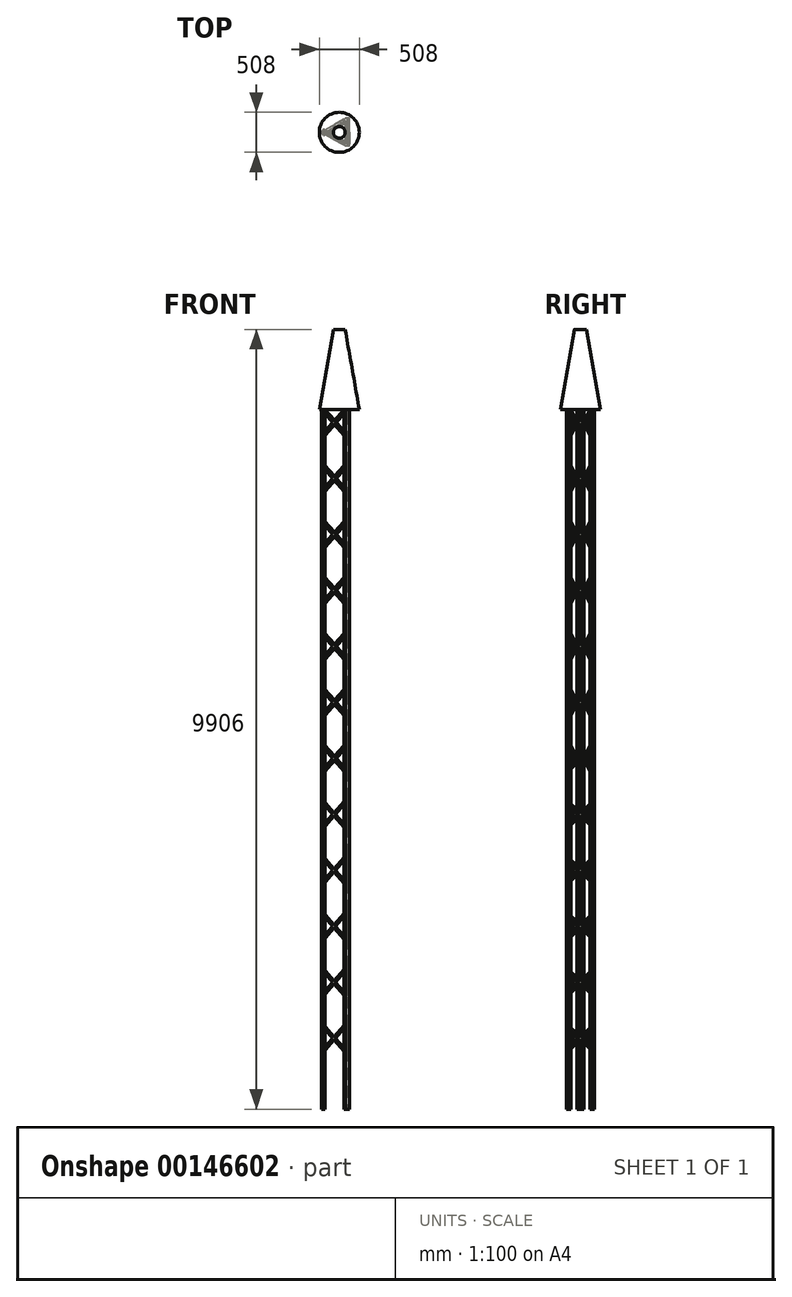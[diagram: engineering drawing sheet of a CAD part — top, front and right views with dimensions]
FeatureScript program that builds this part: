
annotation { "Feature Type Name" : "Feature", "Feature Type Description" : "" }
export const myFeature = defineFeature(function(context is Context, id is Id, definition is map)
    precondition{}
    {
        {
            var Q0;
            Q0=qCreatedBy(makeId("Right.planeOp"),FACE);
            var sketch = newSketch(context, id + "F0", { "sketchPlane" : qUnion([Q0])});
            skLineSegment(sketch, "E0.bottom", {"start": v(0, 1828.8) * mm, "end": v(25.4, 1828.8) * mm});
            skLineSegment(sketch, "E0.top", {"start": v(0, -7061.2) * mm, "end": v(25.4, -7061.2) * mm});
            skLineSegment(sketch, "E0.left", {"start": v(0, 1828.8) * mm, "end": v(0, -7061.2) * mm});
            skLineSegment(sketch, "E0.right", {"start": v(25.4, 1828.8) * mm, "end": v(25.4, -7061.2) * mm});
            skLineSegment(sketch, "E1.bottom", {"start": v(330.2, -7061.2) * mm, "end": v(355.6, -7061.2) * mm});
            skLineSegment(sketch, "E1.top", {"start": v(330.2, 1828.8) * mm, "end": v(355.6, 1828.8) * mm});
            skLineSegment(sketch, "E1.left", {"start": v(330.2, -7061.2) * mm, "end": v(330.2, 1828.8) * mm});
            skLineSegment(sketch, "E1.right", {"start": v(355.6, -7061.2) * mm, "end": v(355.6, 1828.8) * mm});
            skLineSegment(sketch, "E2", {"start": v(25.4, 1828.8) * mm, "end": v(330.2, 1524) * mm});
            skLineSegment(sketch, "E3", {"start": v(25.4, 1803.4) * mm, "end": v(330.2, 1498.6) * mm});
            skLineSegment(sketch, "E4.0.1.0", {"start": v(25.4, 1092.2) * mm, "end": v(330.2, 787.4) * mm});
            skLineSegment(sketch, "E4.0.1.1", {"start": v(25.4, 1117.6) * mm, "end": v(330.2, 812.8) * mm});
            skLineSegment(sketch, "E4.0.2.0", {"start": v(25.4, 381) * mm, "end": v(330.2, 76.2) * mm});
            skLineSegment(sketch, "E4.0.2.1", {"start": v(25.4, 406.4) * mm, "end": v(330.2, 101.6) * mm});
            skLineSegment(sketch, "E4.0.3.0", {"start": v(25.4, -330.2) * mm, "end": v(330.2, -635) * mm});
            skLineSegment(sketch, "E4.0.3.1", {"start": v(25.4, -304.8) * mm, "end": v(330.2, -609.6) * mm});
            skLineSegment(sketch, "E4.0.4.0", {"start": v(25.4, -1041.4) * mm, "end": v(330.2, -1346.2) * mm});
            skLineSegment(sketch, "E4.0.4.1", {"start": v(25.4, -1016) * mm, "end": v(330.2, -1320.8) * mm});
            skLineSegment(sketch, "E4.0.5.0", {"start": v(25.4, -1752.6) * mm, "end": v(330.2, -2057.4) * mm});
            skLineSegment(sketch, "E4.0.5.1", {"start": v(25.4, -1727.2) * mm, "end": v(330.2, -2032) * mm});
            skLineSegment(sketch, "E4.0.6.0", {"start": v(25.4, -2463.8) * mm, "end": v(330.2, -2768.6) * mm});
            skLineSegment(sketch, "E4.0.6.1", {"start": v(25.4, -2438.4) * mm, "end": v(330.2, -2743.2) * mm});
            skLineSegment(sketch, "E4.0.7.0", {"start": v(25.4, -3175) * mm, "end": v(330.2, -3479.8) * mm});
            skLineSegment(sketch, "E4.0.7.1", {"start": v(25.4, -3149.6) * mm, "end": v(330.2, -3454.4) * mm});
            skLineSegment(sketch, "E4.0.8.0", {"start": v(25.4, -3886.2) * mm, "end": v(330.2, -4191) * mm});
            skLineSegment(sketch, "E4.0.8.1", {"start": v(25.4, -3860.8) * mm, "end": v(330.2, -4165.6) * mm});
            skLineSegment(sketch, "E4.0.9.0", {"start": v(25.4, -4597.4) * mm, "end": v(330.2, -4902.2) * mm});
            skLineSegment(sketch, "E4.0.9.1", {"start": v(25.4, -4572) * mm, "end": v(330.2, -4876.8) * mm});
            skLineSegment(sketch, "E4.0.10.0", {"start": v(25.4, -5308.6) * mm, "end": v(330.2, -5613.4) * mm});
            skLineSegment(sketch, "E4.0.10.1", {"start": v(25.4, -5283.2) * mm, "end": v(330.2, -5588) * mm});
            skLineSegment(sketch, "E4.0.11.0", {"start": v(25.4, -6019.8) * mm, "end": v(330.2, -6324.6) * mm});
            skLineSegment(sketch, "E4.0.11.1", {"start": v(25.4, -5994.4) * mm, "end": v(330.2, -6299.2) * mm});
            skLineSegment(sketch, "E4.direction1", {"start": v(330.2, 1498.6) * mm, "end": v(355.6, 1498.6) * mm, "construction": true});
            skLineSegment(sketch, "E4.direction2", {"start": v(330.2, 1498.6) * mm, "end": v(330.2, 787.4) * mm, "construction": true});
            skLineSegment(sketch, "E5", {"start": v(177.8, 1830.45) * mm, "end": v(177.8, 0) * mm});
            skLineSegment(sketch, "E6.MirrorCS", {"start": v(330.2, 1828.8) * mm, "end": v(25.4, 1524) * mm});
            skLineSegment(sketch, "E7.MirrorCS", {"start": v(330.2, 1803.4) * mm, "end": v(25.4, 1498.6) * mm});
            skLineSegment(sketch, "E8.MirrorCS", {"start": v(330.2, 1117.6) * mm, "end": v(25.4, 812.8) * mm});
            skLineSegment(sketch, "E9.MirrorCS", {"start": v(330.2, 1092.2) * mm, "end": v(25.4, 787.4) * mm});
            skLineSegment(sketch, "E10.MirrorCS", {"start": v(330.2, 406.4) * mm, "end": v(25.4, 101.6) * mm});
            skLineSegment(sketch, "E11.MirrorCS", {"start": v(330.2, 381) * mm, "end": v(25.4, 76.2) * mm});
            skLineSegment(sketch, "E12.MirrorCS", {"start": v(330.2, -330.2) * mm, "end": v(25.4, -635) * mm});
            skLineSegment(sketch, "E13.MirrorCS", {"start": v(330.2, -1016) * mm, "end": v(25.4, -1320.8) * mm});
            skLineSegment(sketch, "E14.MirrorCS", {"start": v(330.2, -1041.4) * mm, "end": v(25.4, -1346.2) * mm});
            skLineSegment(sketch, "E15.MirrorCS", {"start": v(330.2, -1727.2) * mm, "end": v(25.4, -2032) * mm});
            skLineSegment(sketch, "E16.MirrorCS", {"start": v(330.2, -1752.6) * mm, "end": v(25.4, -2057.4) * mm});
            skLineSegment(sketch, "E17.MirrorCS", {"start": v(330.2, -304.8) * mm, "end": v(25.4, -609.6) * mm});
            skLineSegment(sketch, "E18.MirrorCS", {"start": v(330.2, -2438.4) * mm, "end": v(25.4, -2743.2) * mm});
            skLineSegment(sketch, "E19.MirrorCS", {"start": v(330.2, -2463.8) * mm, "end": v(25.4, -2768.6) * mm});
            skLineSegment(sketch, "E20.MirrorCS", {"start": v(330.2, -3149.6) * mm, "end": v(25.4, -3454.4) * mm});
            skLineSegment(sketch, "E21.MirrorCS", {"start": v(330.2, -3175) * mm, "end": v(25.4, -3479.8) * mm});
            skLineSegment(sketch, "E22.MirrorCS", {"start": v(330.2, -3860.8) * mm, "end": v(25.4, -4165.6) * mm});
            skLineSegment(sketch, "E23.MirrorCS", {"start": v(330.2, -3886.2) * mm, "end": v(25.4, -4191) * mm});
            skLineSegment(sketch, "E24.MirrorCS", {"start": v(330.2, -4572) * mm, "end": v(25.4, -4876.8) * mm});
            skLineSegment(sketch, "E25.MirrorCS", {"start": v(330.2, -4597.4) * mm, "end": v(25.4, -4902.2) * mm});
            skLineSegment(sketch, "E26.MirrorCS", {"start": v(330.2, -5283.2) * mm, "end": v(25.4, -5588) * mm});
            skLineSegment(sketch, "E27.MirrorCS", {"start": v(330.2, -5308.6) * mm, "end": v(25.4, -5613.4) * mm});
            skLineSegment(sketch, "E28.MirrorCS", {"start": v(330.2, -5994.4) * mm, "end": v(25.4, -6299.2) * mm});
            skLineSegment(sketch, "E29.MirrorCS", {"start": v(330.2, -6019.8) * mm, "end": v(25.4, -6324.6) * mm});
            skSolve(sketch);
        }
        {
            var Q0;
            {var subQ1=sQuery(id+"F0.wireOp",EDGE,"E0.right");var subQ3=sQuery(id+"F0.wireOp",EDGE,"E3");var subQ4=makeQuery(id+"F0.imprint","INTERSECT",VERTEX,{"derivedFrom":[subQ1,subQ3]});Q0=makeQuery(id+"F0.imprint","IMPRINT",FACE,{"disambiguationData":[TD([[makeQuery(id+"F0.imprint","IMPRINT",EDGE,{"disambiguationData":[TD([[subQ4,-1.0]])],"derivedFrom":subQ3}),1.0]])]});}
            var Q1;
            {var subQ30=sQuery(id+"F0.wireOp",EDGE,"E0.bottom");Q1=makeQuery(id+"F0.imprint","IMPRINT",FACE,{"disambiguationData":[TD([[makeQuery(id+"F0.imprint","IMPRINT",EDGE,{"derivedFrom":subQ30}),-1.0]])]});}
            var Q2;
            {var subQ0=sQuery(id+"F0.wireOp",EDGE,"E4.0.1.0");var subQ1=sQuery(id+"F0.wireOp",EDGE,"E0.right");var subQ2=makeQuery(id+"F0.imprint","INTERSECT",VERTEX,{"derivedFrom":[subQ1,subQ0]});Q2=makeQuery(id+"F0.imprint","IMPRINT",FACE,{"disambiguationData":[TD([[makeQuery(id+"F0.imprint","IMPRINT",EDGE,{"disambiguationData":[TD([[subQ2,1.0]])],"derivedFrom":subQ1}),1.0]])]});}
            var Q3;
            {var subQ0=sQuery(id+"F0.wireOp",EDGE,"E8.MirrorCS");var subQ1=sQuery(id+"F0.wireOp",EDGE,"E4.0.1.0");var subQ2=makeQuery(id+"F0.imprint","INTERSECT",VERTEX,{"derivedFrom":[subQ1,subQ0]});Q3=makeQuery(id+"F0.imprint","IMPRINT",FACE,{"disambiguationData":[TD([[makeQuery(id+"F0.imprint","IMPRINT",EDGE,{"disambiguationData":[TD([[subQ2,-1.0]])],"derivedFrom":subQ1}),1.0]])]});}
            var Q4;
            {var subQ0=sQuery(id+"F0.wireOp",EDGE,"E9.MirrorCS");var subQ1=sQuery(id+"F0.wireOp",EDGE,"E4.0.1.1");var subQ2=makeQuery(id+"F0.imprint","INTERSECT",VERTEX,{"derivedFrom":[subQ1,subQ0]});Q4=makeQuery(id+"F0.imprint","IMPRINT",FACE,{"disambiguationData":[TD([[makeQuery(id+"F0.imprint","IMPRINT",EDGE,{"disambiguationData":[TD([[subQ2,1.0]])],"derivedFrom":subQ1}),-1.0]])]});}
            var Q5;
            {var subQ0=sQuery(id+"F0.wireOp",EDGE,"E4.0.1.0");var subQ1=sQuery(id+"F0.wireOp",EDGE,"E1.left");var subQ2=makeQuery(id+"F0.imprint","INTERSECT",VERTEX,{"derivedFrom":[subQ1,subQ0]});Q5=makeQuery(id+"F0.imprint","IMPRINT",FACE,{"disambiguationData":[TD([[makeQuery(id+"F0.imprint","IMPRINT",EDGE,{"disambiguationData":[TD([[subQ2,-1.0]])],"derivedFrom":subQ1}),1.0]])]});}
            var Q6;
            {var subQ0=sQuery(id+"F0.wireOp",EDGE,"E6.MirrorCS");var subQ1=sQuery(id+"F0.wireOp",EDGE,"E3");var subQ2=makeQuery(id+"F0.imprint","INTERSECT",VERTEX,{"derivedFrom":[subQ1,subQ0]});Q6=makeQuery(id+"F0.imprint","IMPRINT",FACE,{"disambiguationData":[TD([[makeQuery(id+"F0.imprint","IMPRINT",EDGE,{"disambiguationData":[TD([[subQ2,-1.0]])],"derivedFrom":subQ1}),1.0]])]});}
            var Q7;
            {var subQ1=sQuery(id+"F0.wireOp",EDGE,"E2");var subQ3=sQuery(id+"F0.wireOp",EDGE,"E7.MirrorCS");var subQ4=makeQuery(id+"F0.imprint","INTERSECT",VERTEX,{"derivedFrom":[subQ1,subQ3]});Q7=makeQuery(id+"F0.imprint","IMPRINT",FACE,{"disambiguationData":[TD([[makeQuery(id+"F0.imprint","IMPRINT",EDGE,{"disambiguationData":[TD([[subQ4,1.0]])],"derivedFrom":subQ1}),-1.0]])]});}
            var Q8;
            {var subQ0=sQuery(id+"F0.wireOp",EDGE,"E2");var subQ1=sQuery(id+"F0.wireOp",EDGE,"E1.left");var subQ2=makeQuery(id+"F0.imprint","INTERSECT",VERTEX,{"derivedFrom":[subQ1,subQ0]});Q8=makeQuery(id+"F0.imprint","IMPRINT",FACE,{"disambiguationData":[TD([[makeQuery(id+"F0.imprint","IMPRINT",EDGE,{"disambiguationData":[TD([[subQ2,1.0]])],"derivedFrom":subQ1}),1.0]])]});}
            var Q9;
            {var subQ42=sQuery(id+"F0.wireOp",EDGE,"E1.bottom");Q9=makeQuery(id+"F0.imprint","IMPRINT",FACE,{"disambiguationData":[TD([[makeQuery(id+"F0.imprint","IMPRINT",EDGE,{"derivedFrom":subQ42}),1.0]])]});}
            var Q10;
            {var subQ0=sQuery(id+"F0.wireOp",EDGE,"E4.0.2.1");var subQ1=sQuery(id+"F0.wireOp",EDGE,"E0.right");var subQ2=makeQuery(id+"F0.imprint","INTERSECT",VERTEX,{"derivedFrom":[subQ1,subQ0]});Q10=makeQuery(id+"F0.imprint","IMPRINT",FACE,{"disambiguationData":[TD([[makeQuery(id+"F0.imprint","IMPRINT",EDGE,{"disambiguationData":[TD([[subQ2,-1.0]])],"derivedFrom":subQ1}),1.0]])]});}
            var Q11;
            {var subQ0=sQuery(id+"F0.wireOp",EDGE,"E4.0.2.1");var subQ1=sQuery(id+"F0.wireOp",EDGE,"E1.left");var subQ2=makeQuery(id+"F0.imprint","INTERSECT",VERTEX,{"derivedFrom":[subQ1,subQ0]});Q11=makeQuery(id+"F0.imprint","IMPRINT",FACE,{"disambiguationData":[TD([[makeQuery(id+"F0.imprint","IMPRINT",EDGE,{"disambiguationData":[TD([[subQ2,1.0]])],"derivedFrom":subQ1}),1.0]])]});}
            var Q12;
            {var subQ0=sQuery(id+"F0.wireOp",EDGE,"E6.MirrorCS");var subQ1=sQuery(id+"F0.wireOp",EDGE,"E0.right");var subQ2=makeQuery(id+"F0.imprint","INTERSECT",VERTEX,{"derivedFrom":[subQ1,subQ0]});Q12=makeQuery(id+"F0.imprint","IMPRINT",FACE,{"disambiguationData":[TD([[makeQuery(id+"F0.imprint","IMPRINT",EDGE,{"disambiguationData":[TD([[subQ2,-1.0]])],"derivedFrom":subQ1}),1.0]])]});}
            var Q13;
            {var subQ0=sQuery(id+"F0.wireOp",EDGE,"E4.0.3.0");var subQ1=sQuery(id+"F0.wireOp",EDGE,"E0.right");var subQ2=makeQuery(id+"F0.imprint","INTERSECT",VERTEX,{"derivedFrom":[subQ1,subQ0]});Q13=makeQuery(id+"F0.imprint","IMPRINT",FACE,{"disambiguationData":[TD([[makeQuery(id+"F0.imprint","IMPRINT",EDGE,{"disambiguationData":[TD([[subQ2,1.0]])],"derivedFrom":subQ1}),1.0]])]});}
            var Q14;
            {var subQ0=sQuery(id+"F0.wireOp",EDGE,"E4.0.3.0");var subQ1=sQuery(id+"F0.wireOp",EDGE,"E1.left");var subQ2=makeQuery(id+"F0.imprint","INTERSECT",VERTEX,{"derivedFrom":[subQ1,subQ0]});Q14=makeQuery(id+"F0.imprint","IMPRINT",FACE,{"disambiguationData":[TD([[makeQuery(id+"F0.imprint","IMPRINT",EDGE,{"disambiguationData":[TD([[subQ2,-1.0]])],"derivedFrom":subQ1}),1.0]])]});}
            var Q15;
            {var subQ0=sQuery(id+"F0.wireOp",EDGE,"E17.MirrorCS");var subQ1=sQuery(id+"F0.wireOp",EDGE,"E4.0.3.0");var subQ2=makeQuery(id+"F0.imprint","INTERSECT",VERTEX,{"derivedFrom":[subQ1,subQ0]});Q15=makeQuery(id+"F0.imprint","IMPRINT",FACE,{"disambiguationData":[TD([[makeQuery(id+"F0.imprint","IMPRINT",EDGE,{"disambiguationData":[TD([[subQ2,-1.0]])],"derivedFrom":subQ1}),1.0]])]});}
            var Q16;
            {var subQ0=sQuery(id+"F0.wireOp",EDGE,"E8.MirrorCS");var subQ1=sQuery(id+"F0.wireOp",EDGE,"E0.right");var subQ2=makeQuery(id+"F0.imprint","INTERSECT",VERTEX,{"derivedFrom":[subQ1,subQ0]});Q16=makeQuery(id+"F0.imprint","IMPRINT",FACE,{"disambiguationData":[TD([[makeQuery(id+"F0.imprint","IMPRINT",EDGE,{"disambiguationData":[TD([[subQ2,-1.0]])],"derivedFrom":subQ1}),1.0]])]});}
            var Q17;
            {var subQ0=sQuery(id+"F0.wireOp",EDGE,"E4.0.2.0");var subQ3=sQuery(id+"F0.wireOp",EDGE,"E10.MirrorCS");var subQ5=makeQuery(id+"F0.imprint","INTERSECT",VERTEX,{"derivedFrom":[subQ3,subQ0]});Q17=makeQuery(id+"F0.imprint","IMPRINT",FACE,{"disambiguationData":[TD([[makeQuery(id+"F0.imprint","IMPRINT",EDGE,{"disambiguationData":[TD([[subQ5,1.0]])],"derivedFrom":subQ3}),1.0]])]});}
            var Q18;
            {var subQ0=sQuery(id+"F0.wireOp",EDGE,"E11.MirrorCS");var subQ1=sQuery(id+"F0.wireOp",EDGE,"E4.0.2.1");var subQ2=makeQuery(id+"F0.imprint","INTERSECT",VERTEX,{"derivedFrom":[subQ1,subQ0]});Q18=makeQuery(id+"F0.imprint","IMPRINT",FACE,{"disambiguationData":[TD([[makeQuery(id+"F0.imprint","IMPRINT",EDGE,{"disambiguationData":[TD([[subQ2,1.0]])],"derivedFrom":subQ1}),-1.0]])]});}
            var Q19;
            {var subQ1=sQuery(id+"F0.wireOp",EDGE,"E1.left");var subQ3=sQuery(id+"F0.wireOp",EDGE,"E7.MirrorCS");var subQ4=makeQuery(id+"F0.imprint","INTERSECT",VERTEX,{"derivedFrom":[subQ1,subQ3]});Q19=makeQuery(id+"F0.imprint","IMPRINT",FACE,{"disambiguationData":[TD([[makeQuery(id+"F0.imprint","IMPRINT",EDGE,{"disambiguationData":[TD([[subQ4,-1.0]])],"derivedFrom":subQ3}),-1.0]])]});}
            var Q20;
            {var subQ0=sQuery(id+"F0.wireOp",EDGE,"E8.MirrorCS");var subQ1=sQuery(id+"F0.wireOp",EDGE,"E1.left");var subQ2=makeQuery(id+"F0.imprint","INTERSECT",VERTEX,{"derivedFrom":[subQ1,subQ0]});Q20=makeQuery(id+"F0.imprint","IMPRINT",FACE,{"disambiguationData":[TD([[makeQuery(id+"F0.imprint","IMPRINT",EDGE,{"disambiguationData":[TD([[subQ2,1.0]])],"derivedFrom":subQ1}),1.0]])]});}
            var Q21;
            {var subQ0=sQuery(id+"F0.wireOp",EDGE,"E10.MirrorCS");var subQ1=sQuery(id+"F0.wireOp",EDGE,"E1.left");var subQ2=makeQuery(id+"F0.imprint","INTERSECT",VERTEX,{"derivedFrom":[subQ1,subQ0]});Q21=makeQuery(id+"F0.imprint","IMPRINT",FACE,{"disambiguationData":[TD([[makeQuery(id+"F0.imprint","IMPRINT",EDGE,{"disambiguationData":[TD([[subQ2,1.0]])],"derivedFrom":subQ1}),1.0]])]});}
            var Q22;
            {var subQ0=sQuery(id+"F0.wireOp",EDGE,"E12.MirrorCS");var subQ1=sQuery(id+"F0.wireOp",EDGE,"E1.left");var subQ2=makeQuery(id+"F0.imprint","INTERSECT",VERTEX,{"derivedFrom":[subQ1,subQ0]});Q22=makeQuery(id+"F0.imprint","IMPRINT",FACE,{"disambiguationData":[TD([[makeQuery(id+"F0.imprint","IMPRINT",EDGE,{"disambiguationData":[TD([[subQ2,-1.0]])],"derivedFrom":subQ1}),1.0]])]});}
            var Q23;
            {var subQ0=sQuery(id+"F0.wireOp",EDGE,"E4.0.4.0");var subQ1=sQuery(id+"F0.wireOp",EDGE,"E0.right");var subQ2=makeQuery(id+"F0.imprint","INTERSECT",VERTEX,{"derivedFrom":[subQ1,subQ0]});Q23=makeQuery(id+"F0.imprint","IMPRINT",FACE,{"disambiguationData":[TD([[makeQuery(id+"F0.imprint","IMPRINT",EDGE,{"disambiguationData":[TD([[subQ2,1.0]])],"derivedFrom":subQ1}),1.0]])]});}
            var Q24;
            {var subQ0=sQuery(id+"F0.wireOp",EDGE,"E4.0.4.0");var subQ1=sQuery(id+"F0.wireOp",EDGE,"E1.left");var subQ2=makeQuery(id+"F0.imprint","INTERSECT",VERTEX,{"derivedFrom":[subQ1,subQ0]});Q24=makeQuery(id+"F0.imprint","IMPRINT",FACE,{"disambiguationData":[TD([[makeQuery(id+"F0.imprint","IMPRINT",EDGE,{"disambiguationData":[TD([[subQ2,-1.0]])],"derivedFrom":subQ1}),1.0]])]});}
            var Q25;
            {var subQ0=sQuery(id+"F0.wireOp",EDGE,"E13.MirrorCS");var subQ1=sQuery(id+"F0.wireOp",EDGE,"E4.0.4.0");var subQ2=makeQuery(id+"F0.imprint","INTERSECT",VERTEX,{"derivedFrom":[subQ1,subQ0]});Q25=makeQuery(id+"F0.imprint","IMPRINT",FACE,{"disambiguationData":[TD([[makeQuery(id+"F0.imprint","IMPRINT",EDGE,{"disambiguationData":[TD([[subQ2,-1.0]])],"derivedFrom":subQ1}),1.0]])]});}
            var Q26;
            {var subQ0=sQuery(id+"F0.wireOp",EDGE,"E10.MirrorCS");var subQ1=sQuery(id+"F0.wireOp",EDGE,"E0.right");var subQ2=makeQuery(id+"F0.imprint","INTERSECT",VERTEX,{"derivedFrom":[subQ1,subQ0]});Q26=makeQuery(id+"F0.imprint","IMPRINT",FACE,{"disambiguationData":[TD([[makeQuery(id+"F0.imprint","IMPRINT",EDGE,{"disambiguationData":[TD([[subQ2,-1.0]])],"derivedFrom":subQ1}),1.0]])]});}
            var Q27;
            {var subQ0=sQuery(id+"F0.wireOp",EDGE,"E13.MirrorCS");var subQ1=sQuery(id+"F0.wireOp",EDGE,"E1.left");var subQ2=makeQuery(id+"F0.imprint","INTERSECT",VERTEX,{"derivedFrom":[subQ1,subQ0]});Q27=makeQuery(id+"F0.imprint","IMPRINT",FACE,{"disambiguationData":[TD([[makeQuery(id+"F0.imprint","IMPRINT",EDGE,{"disambiguationData":[TD([[subQ2,1.0]])],"derivedFrom":subQ1}),1.0]])]});}
            var Q28;
            {var subQ0=sQuery(id+"F0.wireOp",EDGE,"E15.MirrorCS");var subQ1=sQuery(id+"F0.wireOp",EDGE,"E1.left");var subQ2=makeQuery(id+"F0.imprint","INTERSECT",VERTEX,{"derivedFrom":[subQ1,subQ0]});Q28=makeQuery(id+"F0.imprint","IMPRINT",FACE,{"disambiguationData":[TD([[makeQuery(id+"F0.imprint","IMPRINT",EDGE,{"disambiguationData":[TD([[subQ2,1.0]])],"derivedFrom":subQ1}),1.0]])]});}
            var Q29;
            {var subQ0=sQuery(id+"F0.wireOp",EDGE,"E18.MirrorCS");var subQ1=sQuery(id+"F0.wireOp",EDGE,"E1.left");var subQ2=makeQuery(id+"F0.imprint","INTERSECT",VERTEX,{"derivedFrom":[subQ1,subQ0]});Q29=makeQuery(id+"F0.imprint","IMPRINT",FACE,{"disambiguationData":[TD([[makeQuery(id+"F0.imprint","IMPRINT",EDGE,{"disambiguationData":[TD([[subQ2,1.0]])],"derivedFrom":subQ1}),1.0]])]});}
            var Q30;
            {var subQ0=sQuery(id+"F0.wireOp",EDGE,"E4.0.5.0");var subQ1=sQuery(id+"F0.wireOp",EDGE,"E0.right");var subQ2=makeQuery(id+"F0.imprint","INTERSECT",VERTEX,{"derivedFrom":[subQ1,subQ0]});Q30=makeQuery(id+"F0.imprint","IMPRINT",FACE,{"disambiguationData":[TD([[makeQuery(id+"F0.imprint","IMPRINT",EDGE,{"disambiguationData":[TD([[subQ2,1.0]])],"derivedFrom":subQ1}),1.0]])]});}
            var Q31;
            {var subQ0=sQuery(id+"F0.wireOp",EDGE,"E4.0.5.0");var subQ1=sQuery(id+"F0.wireOp",EDGE,"E1.left");var subQ2=makeQuery(id+"F0.imprint","INTERSECT",VERTEX,{"derivedFrom":[subQ1,subQ0]});Q31=makeQuery(id+"F0.imprint","IMPRINT",FACE,{"disambiguationData":[TD([[makeQuery(id+"F0.imprint","IMPRINT",EDGE,{"disambiguationData":[TD([[subQ2,-1.0]])],"derivedFrom":subQ1}),1.0]])]});}
            var Q32;
            {var subQ0=sQuery(id+"F0.wireOp",EDGE,"E15.MirrorCS");var subQ1=sQuery(id+"F0.wireOp",EDGE,"E4.0.5.0");var subQ2=makeQuery(id+"F0.imprint","INTERSECT",VERTEX,{"derivedFrom":[subQ1,subQ0]});Q32=makeQuery(id+"F0.imprint","IMPRINT",FACE,{"disambiguationData":[TD([[makeQuery(id+"F0.imprint","IMPRINT",EDGE,{"disambiguationData":[TD([[subQ2,-1.0]])],"derivedFrom":subQ1}),1.0]])]});}
            var Q33;
            {var subQ0=sQuery(id+"F0.wireOp",EDGE,"E12.MirrorCS");var subQ1=sQuery(id+"F0.wireOp",EDGE,"E0.right");var subQ2=makeQuery(id+"F0.imprint","INTERSECT",VERTEX,{"derivedFrom":[subQ1,subQ0]});Q33=makeQuery(id+"F0.imprint","IMPRINT",FACE,{"disambiguationData":[TD([[makeQuery(id+"F0.imprint","IMPRINT",EDGE,{"disambiguationData":[TD([[subQ2,1.0]])],"derivedFrom":subQ1}),1.0]])]});}
            var Q34;
            {var subQ0=sQuery(id+"F0.wireOp",EDGE,"E4.0.6.0");var subQ1=sQuery(id+"F0.wireOp",EDGE,"E0.right");var subQ2=makeQuery(id+"F0.imprint","INTERSECT",VERTEX,{"derivedFrom":[subQ1,subQ0]});Q34=makeQuery(id+"F0.imprint","IMPRINT",FACE,{"disambiguationData":[TD([[makeQuery(id+"F0.imprint","IMPRINT",EDGE,{"disambiguationData":[TD([[subQ2,1.0]])],"derivedFrom":subQ1}),1.0]])]});}
            var Q35;
            {var subQ0=sQuery(id+"F0.wireOp",EDGE,"E4.0.6.0");var subQ1=sQuery(id+"F0.wireOp",EDGE,"E1.left");var subQ2=makeQuery(id+"F0.imprint","INTERSECT",VERTEX,{"derivedFrom":[subQ1,subQ0]});Q35=makeQuery(id+"F0.imprint","IMPRINT",FACE,{"disambiguationData":[TD([[makeQuery(id+"F0.imprint","IMPRINT",EDGE,{"disambiguationData":[TD([[subQ2,-1.0]])],"derivedFrom":subQ1}),1.0]])]});}
            var Q36;
            {var subQ0=sQuery(id+"F0.wireOp",EDGE,"E18.MirrorCS");var subQ1=sQuery(id+"F0.wireOp",EDGE,"E4.0.6.0");var subQ2=makeQuery(id+"F0.imprint","INTERSECT",VERTEX,{"derivedFrom":[subQ1,subQ0]});Q36=makeQuery(id+"F0.imprint","IMPRINT",FACE,{"disambiguationData":[TD([[makeQuery(id+"F0.imprint","IMPRINT",EDGE,{"disambiguationData":[TD([[subQ2,-1.0]])],"derivedFrom":subQ1}),1.0]])]});}
            var Q37;
            {var subQ0=sQuery(id+"F0.wireOp",EDGE,"E13.MirrorCS");var subQ1=sQuery(id+"F0.wireOp",EDGE,"E0.right");var subQ2=makeQuery(id+"F0.imprint","INTERSECT",VERTEX,{"derivedFrom":[subQ1,subQ0]});Q37=makeQuery(id+"F0.imprint","IMPRINT",FACE,{"disambiguationData":[TD([[makeQuery(id+"F0.imprint","IMPRINT",EDGE,{"disambiguationData":[TD([[subQ2,-1.0]])],"derivedFrom":subQ1}),1.0]])]});}
            var Q38;
            {var subQ0=sQuery(id+"F0.wireOp",EDGE,"E15.MirrorCS");var subQ1=sQuery(id+"F0.wireOp",EDGE,"E0.right");var subQ2=makeQuery(id+"F0.imprint","INTERSECT",VERTEX,{"derivedFrom":[subQ1,subQ0]});Q38=makeQuery(id+"F0.imprint","IMPRINT",FACE,{"disambiguationData":[TD([[makeQuery(id+"F0.imprint","IMPRINT",EDGE,{"disambiguationData":[TD([[subQ2,-1.0]])],"derivedFrom":subQ1}),1.0]])]});}
            var Q39;
            {var subQ0=sQuery(id+"F0.wireOp",EDGE,"E12.MirrorCS");var subQ1=sQuery(id+"F0.wireOp",EDGE,"E4.0.3.1");var subQ2=makeQuery(id+"F0.imprint","INTERSECT",VERTEX,{"derivedFrom":[subQ1,subQ0]});Q39=makeQuery(id+"F0.imprint","IMPRINT",FACE,{"disambiguationData":[TD([[makeQuery(id+"F0.imprint","IMPRINT",EDGE,{"disambiguationData":[TD([[subQ2,1.0]])],"derivedFrom":subQ1}),-1.0]])]});}
            extrude(context, id + "F1", {"entities" : qUnion([Q0, Q1, Q2, Q3, Q4, Q5, Q6, Q7, Q8, Q9, Q10, Q11, Q12, Q13, Q14, Q15, Q16, Q17, Q18, Q19, Q20, Q21, Q22, Q23, Q24, Q25, Q26, Q27, Q28, Q29, Q30, Q31, Q32, Q33, Q34, Q35, Q36, Q37, Q38, Q39]), "depth" : 25.4 * mm});
        }
        {
            var Q0;
            {var subQ0=sQuery(id+"F0.wireOp",EDGE,"E14.MirrorCS");var subQ1=sQuery(id+"F0.wireOp",EDGE,"E4.0.5.0");var subQ2=makeQuery(id+"F0.imprint","INTERSECT",VERTEX,{"derivedFrom":[subQ1,subQ0]});Q0=makeQuery(id+"F0.imprint","IMPRINT",FACE,{"disambiguationData":[TD([[makeQuery(id+"F0.imprint","IMPRINT",EDGE,{"disambiguationData":[TD([[subQ2,-1.0]])],"derivedFrom":subQ1}),1.0]])]});}
            var Q1;
            {var subQ0=sQuery(id+"F0.wireOp",EDGE,"E15.MirrorCS");var subQ1=sQuery(id+"F0.wireOp",EDGE,"E4.0.5.0");var subQ2=makeQuery(id+"F0.imprint","INTERSECT",VERTEX,{"derivedFrom":[subQ1,subQ0]});Q1=makeQuery(id+"F0.imprint","IMPRINT",FACE,{"disambiguationData":[TD([[makeQuery(id+"F0.imprint","IMPRINT",EDGE,{"disambiguationData":[TD([[subQ2,-1.0]])],"derivedFrom":subQ1}),1.0]])]});}
            var Q2;
            {var subQ0=sQuery(id+"F0.wireOp",EDGE,"E16.MirrorCS");var subQ1=sQuery(id+"F0.wireOp",EDGE,"E4.0.5.1");var subQ2=makeQuery(id+"F0.imprint","INTERSECT",VERTEX,{"derivedFrom":[subQ1,subQ0]});Q2=makeQuery(id+"F0.imprint","IMPRINT",FACE,{"disambiguationData":[TD([[makeQuery(id+"F0.imprint","IMPRINT",EDGE,{"disambiguationData":[TD([[subQ2,1.0]])],"derivedFrom":subQ1}),-1.0]])]});}
            var Q3;
            {var subQ0=sQuery(id+"F0.wireOp",EDGE,"E15.MirrorCS");var subQ1=sQuery(id+"F0.wireOp",EDGE,"E4.0.6.0");var subQ2=makeQuery(id+"F0.imprint","INTERSECT",VERTEX,{"derivedFrom":[subQ1,subQ0]});Q3=makeQuery(id+"F0.imprint","IMPRINT",FACE,{"disambiguationData":[TD([[makeQuery(id+"F0.imprint","IMPRINT",EDGE,{"disambiguationData":[TD([[subQ2,-1.0]])],"derivedFrom":subQ1}),1.0]])]});}
            var Q4;
            {var subQ0=sQuery(id+"F0.wireOp",EDGE,"E15.MirrorCS");var subQ1=sQuery(id+"F0.wireOp",EDGE,"E4.0.7.0");var subQ2=makeQuery(id+"F0.imprint","INTERSECT",VERTEX,{"derivedFrom":[subQ1,subQ0]});Q4=makeQuery(id+"F0.imprint","IMPRINT",FACE,{"disambiguationData":[TD([[makeQuery(id+"F0.imprint","IMPRINT",EDGE,{"disambiguationData":[TD([[subQ2,-1.0]])],"derivedFrom":subQ1}),1.0]])]});}
            var Q5;
            {var subQ0=sQuery(id+"F0.wireOp",EDGE,"E15.MirrorCS");var subQ1=sQuery(id+"F0.wireOp",EDGE,"E0.right");var subQ2=makeQuery(id+"F0.imprint","INTERSECT",VERTEX,{"derivedFrom":[subQ1,subQ0]});Q5=makeQuery(id+"F0.imprint","IMPRINT",FACE,{"disambiguationData":[TD([[makeQuery(id+"F0.imprint","IMPRINT",EDGE,{"disambiguationData":[TD([[subQ2,-1.0]])],"derivedFrom":subQ1}),1.0]])]});}
            var Q6;
            {var subQ0=sQuery(id+"F0.wireOp",EDGE,"E4.0.7.0");var subQ1=sQuery(id+"F0.wireOp",EDGE,"E0.right");var subQ2=makeQuery(id+"F0.imprint","INTERSECT",VERTEX,{"derivedFrom":[subQ1,subQ0]});Q6=makeQuery(id+"F0.imprint","IMPRINT",FACE,{"disambiguationData":[TD([[makeQuery(id+"F0.imprint","IMPRINT",EDGE,{"disambiguationData":[TD([[subQ2,1.0]])],"derivedFrom":subQ1}),1.0]])]});}
            var Q7;
            {var subQ0=sQuery(id+"F0.wireOp",EDGE,"E14.MirrorCS");var subQ1=sQuery(id+"F0.wireOp",EDGE,"E4.0.6.0");var subQ2=makeQuery(id+"F0.imprint","INTERSECT",VERTEX,{"derivedFrom":[subQ1,subQ0]});Q7=makeQuery(id+"F0.imprint","IMPRINT",FACE,{"disambiguationData":[TD([[makeQuery(id+"F0.imprint","IMPRINT",EDGE,{"disambiguationData":[TD([[subQ2,-1.0]])],"derivedFrom":subQ1}),1.0]])]});}
            var Q8;
            {var subQ0=sQuery(id+"F0.wireOp",EDGE,"E16.MirrorCS");var subQ1=sQuery(id+"F0.wireOp",EDGE,"E4.0.6.0");var subQ2=makeQuery(id+"F0.imprint","INTERSECT",VERTEX,{"derivedFrom":[subQ1,subQ0]});Q8=makeQuery(id+"F0.imprint","IMPRINT",FACE,{"disambiguationData":[TD([[makeQuery(id+"F0.imprint","IMPRINT",EDGE,{"disambiguationData":[TD([[subQ2,-1.0]])],"derivedFrom":subQ1}),1.0]])]});}
            var Q9;
            {var subQ0=sQuery(id+"F0.wireOp",EDGE,"E18.MirrorCS");var subQ1=sQuery(id+"F0.wireOp",EDGE,"E4.0.6.0");var subQ2=makeQuery(id+"F0.imprint","INTERSECT",VERTEX,{"derivedFrom":[subQ1,subQ0]});Q9=makeQuery(id+"F0.imprint","IMPRINT",FACE,{"disambiguationData":[TD([[makeQuery(id+"F0.imprint","IMPRINT",EDGE,{"disambiguationData":[TD([[subQ2,-1.0]])],"derivedFrom":subQ1}),1.0]])]});}
            var Q10;
            {var subQ0=sQuery(id+"F0.wireOp",EDGE,"E19.MirrorCS");var subQ1=sQuery(id+"F0.wireOp",EDGE,"E4.0.6.1");var subQ2=makeQuery(id+"F0.imprint","INTERSECT",VERTEX,{"derivedFrom":[subQ1,subQ0]});Q10=makeQuery(id+"F0.imprint","IMPRINT",FACE,{"disambiguationData":[TD([[makeQuery(id+"F0.imprint","IMPRINT",EDGE,{"disambiguationData":[TD([[subQ2,1.0]])],"derivedFrom":subQ1}),-1.0]])]});}
            var Q11;
            {var subQ0=sQuery(id+"F0.wireOp",EDGE,"E18.MirrorCS");var subQ1=sQuery(id+"F0.wireOp",EDGE,"E4.0.5.0");var subQ2=makeQuery(id+"F0.imprint","INTERSECT",VERTEX,{"derivedFrom":[subQ1,subQ0]});Q11=makeQuery(id+"F0.imprint","IMPRINT",FACE,{"disambiguationData":[TD([[makeQuery(id+"F0.imprint","IMPRINT",EDGE,{"disambiguationData":[TD([[subQ2,-1.0]])],"derivedFrom":subQ1}),1.0]])]});}
            var Q12;
            {var subQ3=sQuery(id+"F0.wireOp",EDGE,"E16.MirrorCS");var subQ5=sQuery(id+"F0.wireOp",EDGE,"E4.0.5.1");var subQ6=makeQuery(id+"F0.imprint","INTERSECT",VERTEX,{"derivedFrom":[subQ5,subQ3]});Q12=makeQuery(id+"F0.imprint","IMPRINT",FACE,{"disambiguationData":[TD([[makeQuery(id+"F0.imprint","IMPRINT",EDGE,{"disambiguationData":[TD([[subQ6,-1.0]])],"derivedFrom":subQ5}),-1.0]])]});}
            var Q13;
            {var subQ0=sQuery(id+"F0.wireOp",EDGE,"E19.MirrorCS");var subQ1=sQuery(id+"F0.wireOp",EDGE,"E4.0.5.0");var subQ2=makeQuery(id+"F0.imprint","INTERSECT",VERTEX,{"derivedFrom":[subQ1,subQ0]});Q13=makeQuery(id+"F0.imprint","IMPRINT",FACE,{"disambiguationData":[TD([[makeQuery(id+"F0.imprint","IMPRINT",EDGE,{"disambiguationData":[TD([[subQ2,-1.0]])],"derivedFrom":subQ1}),1.0]])]});}
            var Q14;
            {var subQ0=sQuery(id+"F0.wireOp",EDGE,"E21.MirrorCS");var subQ1=sQuery(id+"F0.wireOp",EDGE,"E1.left");var subQ2=makeQuery(id+"F0.imprint","INTERSECT",VERTEX,{"derivedFrom":[subQ1,subQ0]});Q14=makeQuery(id+"F0.imprint","IMPRINT",FACE,{"disambiguationData":[TD([[makeQuery(id+"F0.imprint","IMPRINT",EDGE,{"disambiguationData":[TD([[subQ2,-1.0]])],"derivedFrom":subQ1}),1.0]])]});}
            var Q15;
            {var subQ0=sQuery(id+"F0.wireOp",EDGE,"E20.MirrorCS");var subQ1=sQuery(id+"F0.wireOp",EDGE,"E4.0.5.0");var subQ2=makeQuery(id+"F0.imprint","INTERSECT",VERTEX,{"derivedFrom":[subQ1,subQ0]});Q15=makeQuery(id+"F0.imprint","IMPRINT",FACE,{"disambiguationData":[TD([[makeQuery(id+"F0.imprint","IMPRINT",EDGE,{"disambiguationData":[TD([[subQ2,-1.0]])],"derivedFrom":subQ1}),1.0]])]});}
            var Q16;
            {var subQ0=sQuery(id+"F0.wireOp",EDGE,"E16.MirrorCS");var subQ1=sQuery(id+"F0.wireOp",EDGE,"E4.0.7.0");var subQ2=makeQuery(id+"F0.imprint","INTERSECT",VERTEX,{"derivedFrom":[subQ1,subQ0]});Q16=makeQuery(id+"F0.imprint","IMPRINT",FACE,{"disambiguationData":[TD([[makeQuery(id+"F0.imprint","IMPRINT",EDGE,{"disambiguationData":[TD([[subQ2,-1.0]])],"derivedFrom":subQ1}),1.0]])]});}
            var Q17;
            {var subQ0=sQuery(id+"F0.wireOp",EDGE,"E18.MirrorCS");var subQ1=sQuery(id+"F0.wireOp",EDGE,"E4.0.7.0");var subQ2=makeQuery(id+"F0.imprint","INTERSECT",VERTEX,{"derivedFrom":[subQ1,subQ0]});Q17=makeQuery(id+"F0.imprint","IMPRINT",FACE,{"disambiguationData":[TD([[makeQuery(id+"F0.imprint","IMPRINT",EDGE,{"disambiguationData":[TD([[subQ2,-1.0]])],"derivedFrom":subQ1}),1.0]])]});}
            var Q18;
            {var subQ0=sQuery(id+"F0.wireOp",EDGE,"E19.MirrorCS");var subQ1=sQuery(id+"F0.wireOp",EDGE,"E4.0.7.0");var subQ2=makeQuery(id+"F0.imprint","INTERSECT",VERTEX,{"derivedFrom":[subQ1,subQ0]});Q18=makeQuery(id+"F0.imprint","IMPRINT",FACE,{"disambiguationData":[TD([[makeQuery(id+"F0.imprint","IMPRINT",EDGE,{"disambiguationData":[TD([[subQ2,-1.0]])],"derivedFrom":subQ1}),1.0]])]});}
            var Q19;
            {var subQ0=sQuery(id+"F0.wireOp",EDGE,"E20.MirrorCS");var subQ1=sQuery(id+"F0.wireOp",EDGE,"E4.0.7.0");var subQ2=makeQuery(id+"F0.imprint","INTERSECT",VERTEX,{"derivedFrom":[subQ1,subQ0]});Q19=makeQuery(id+"F0.imprint","IMPRINT",FACE,{"disambiguationData":[TD([[makeQuery(id+"F0.imprint","IMPRINT",EDGE,{"disambiguationData":[TD([[subQ2,-1.0]])],"derivedFrom":subQ1}),1.0]])]});}
            var Q20;
            {var subQ0=sQuery(id+"F0.wireOp",EDGE,"E21.MirrorCS");var subQ1=sQuery(id+"F0.wireOp",EDGE,"E4.0.7.1");var subQ2=makeQuery(id+"F0.imprint","INTERSECT",VERTEX,{"derivedFrom":[subQ1,subQ0]});Q20=makeQuery(id+"F0.imprint","IMPRINT",FACE,{"disambiguationData":[TD([[makeQuery(id+"F0.imprint","IMPRINT",EDGE,{"disambiguationData":[TD([[subQ2,1.0]])],"derivedFrom":subQ1}),-1.0]])]});}
            var Q21;
            {var subQ3=sQuery(id+"F0.wireOp",EDGE,"E21.MirrorCS");var subQ5=sQuery(id+"F0.wireOp",EDGE,"E4.0.7.1");var subQ6=makeQuery(id+"F0.imprint","INTERSECT",VERTEX,{"derivedFrom":[subQ5,subQ3]});Q21=makeQuery(id+"F0.imprint","IMPRINT",FACE,{"disambiguationData":[TD([[makeQuery(id+"F0.imprint","IMPRINT",EDGE,{"disambiguationData":[TD([[subQ6,-1.0]])],"derivedFrom":subQ5}),-1.0]])]});}
            var Q22;
            {var subQ0=sQuery(id+"F0.wireOp",EDGE,"E22.MirrorCS");var subQ1=sQuery(id+"F0.wireOp",EDGE,"E4.0.7.0");var subQ2=makeQuery(id+"F0.imprint","INTERSECT",VERTEX,{"derivedFrom":[subQ1,subQ0]});Q22=makeQuery(id+"F0.imprint","IMPRINT",FACE,{"disambiguationData":[TD([[makeQuery(id+"F0.imprint","IMPRINT",EDGE,{"disambiguationData":[TD([[subQ2,-1.0]])],"derivedFrom":subQ1}),1.0]])]});}
            var Q23;
            {var subQ0=sQuery(id+"F0.wireOp",EDGE,"E23.MirrorCS");var subQ1=sQuery(id+"F0.wireOp",EDGE,"E4.0.7.0");var subQ2=makeQuery(id+"F0.imprint","INTERSECT",VERTEX,{"derivedFrom":[subQ1,subQ0]});Q23=makeQuery(id+"F0.imprint","IMPRINT",FACE,{"disambiguationData":[TD([[makeQuery(id+"F0.imprint","IMPRINT",EDGE,{"disambiguationData":[TD([[subQ2,-1.0]])],"derivedFrom":subQ1}),1.0]])]});}
            var Q24;
            {var subQ0=sQuery(id+"F0.wireOp",EDGE,"E24.MirrorCS");var subQ1=sQuery(id+"F0.wireOp",EDGE,"E4.0.7.0");var subQ2=makeQuery(id+"F0.imprint","INTERSECT",VERTEX,{"derivedFrom":[subQ1,subQ0]});Q24=makeQuery(id+"F0.imprint","IMPRINT",FACE,{"disambiguationData":[TD([[makeQuery(id+"F0.imprint","IMPRINT",EDGE,{"disambiguationData":[TD([[subQ2,-1.0]])],"derivedFrom":subQ1}),1.0]])]});}
            var Q25;
            {var subQ0=sQuery(id+"F0.wireOp",EDGE,"E4.0.7.0");var subQ1=sQuery(id+"F0.wireOp",EDGE,"E1.left");var subQ2=makeQuery(id+"F0.imprint","INTERSECT",VERTEX,{"derivedFrom":[subQ1,subQ0]});Q25=makeQuery(id+"F0.imprint","IMPRINT",FACE,{"disambiguationData":[TD([[makeQuery(id+"F0.imprint","IMPRINT",EDGE,{"disambiguationData":[TD([[subQ2,-1.0]])],"derivedFrom":subQ1}),1.0]])]});}
            var Q26;
            {var subQ0=sQuery(id+"F0.wireOp",EDGE,"E23.MirrorCS");var subQ1=sQuery(id+"F0.wireOp",EDGE,"E4.0.7.0");var subQ2=makeQuery(id+"F0.imprint","INTERSECT",VERTEX,{"derivedFrom":[subQ1,subQ0]});Q26=makeQuery(id+"F0.imprint","IMPRINT",FACE,{"disambiguationData":[TD([[makeQuery(id+"F0.imprint","IMPRINT",EDGE,{"disambiguationData":[TD([[subQ2,-1.0]])],"derivedFrom":subQ1}),1.0]])]});}
            var Q27;
            {var subQ0=sQuery(id+"F0.wireOp",EDGE,"E24.MirrorCS");var subQ1=sQuery(id+"F0.wireOp",EDGE,"E1.left");var subQ2=makeQuery(id+"F0.imprint","INTERSECT",VERTEX,{"derivedFrom":[subQ1,subQ0]});Q27=makeQuery(id+"F0.imprint","IMPRINT",FACE,{"disambiguationData":[TD([[makeQuery(id+"F0.imprint","IMPRINT",EDGE,{"disambiguationData":[TD([[subQ2,1.0]])],"derivedFrom":subQ1}),1.0]])]});}
            var Q28;
            {var subQ0=sQuery(id+"F0.wireOp",EDGE,"E4.0.6.0");var subQ1=sQuery(id+"F0.wireOp",EDGE,"E1.left");var subQ2=makeQuery(id+"F0.imprint","INTERSECT",VERTEX,{"derivedFrom":[subQ1,subQ0]});Q28=makeQuery(id+"F0.imprint","IMPRINT",FACE,{"disambiguationData":[TD([[makeQuery(id+"F0.imprint","IMPRINT",EDGE,{"disambiguationData":[TD([[subQ2,-1.0]])],"derivedFrom":subQ1}),1.0]])]});}
            var Q29;
            {var subQ0=sQuery(id+"F0.wireOp",EDGE,"E22.MirrorCS");var subQ1=sQuery(id+"F0.wireOp",EDGE,"E4.0.6.0");var subQ2=makeQuery(id+"F0.imprint","INTERSECT",VERTEX,{"derivedFrom":[subQ1,subQ0]});Q29=makeQuery(id+"F0.imprint","IMPRINT",FACE,{"disambiguationData":[TD([[makeQuery(id+"F0.imprint","IMPRINT",EDGE,{"disambiguationData":[TD([[subQ2,-1.0]])],"derivedFrom":subQ1}),1.0]])]});}
            var Q30;
            {var subQ0=sQuery(id+"F0.wireOp",EDGE,"E22.MirrorCS");var subQ1=sQuery(id+"F0.wireOp",EDGE,"E1.left");var subQ2=makeQuery(id+"F0.imprint","INTERSECT",VERTEX,{"derivedFrom":[subQ1,subQ0]});Q30=makeQuery(id+"F0.imprint","IMPRINT",FACE,{"disambiguationData":[TD([[makeQuery(id+"F0.imprint","IMPRINT",EDGE,{"disambiguationData":[TD([[subQ2,1.0]])],"derivedFrom":subQ1}),1.0]])]});}
            var Q31;
            {var subQ0=sQuery(id+"F0.wireOp",EDGE,"E4.0.5.0");var subQ1=sQuery(id+"F0.wireOp",EDGE,"E1.left");var subQ2=makeQuery(id+"F0.imprint","INTERSECT",VERTEX,{"derivedFrom":[subQ1,subQ0]});Q31=makeQuery(id+"F0.imprint","IMPRINT",FACE,{"disambiguationData":[TD([[makeQuery(id+"F0.imprint","IMPRINT",EDGE,{"disambiguationData":[TD([[subQ2,-1.0]])],"derivedFrom":subQ1}),1.0]])]});}
            var Q32;
            {var subQ0=sQuery(id+"F0.wireOp",EDGE,"E21.MirrorCS");var subQ1=sQuery(id+"F0.wireOp",EDGE,"E4.0.6.0");var subQ2=makeQuery(id+"F0.imprint","INTERSECT",VERTEX,{"derivedFrom":[subQ1,subQ0]});Q32=makeQuery(id+"F0.imprint","IMPRINT",FACE,{"disambiguationData":[TD([[makeQuery(id+"F0.imprint","IMPRINT",EDGE,{"disambiguationData":[TD([[subQ2,-1.0]])],"derivedFrom":subQ1}),1.0]])]});}
            var Q33;
            {var subQ0=sQuery(id+"F0.wireOp",EDGE,"E20.MirrorCS");var subQ1=sQuery(id+"F0.wireOp",EDGE,"E4.0.6.0");var subQ2=makeQuery(id+"F0.imprint","INTERSECT",VERTEX,{"derivedFrom":[subQ1,subQ0]});Q33=makeQuery(id+"F0.imprint","IMPRINT",FACE,{"disambiguationData":[TD([[makeQuery(id+"F0.imprint","IMPRINT",EDGE,{"disambiguationData":[TD([[subQ2,-1.0]])],"derivedFrom":subQ1}),1.0]])]});}
            var Q34;
            {var subQ3=sQuery(id+"F0.wireOp",EDGE,"E19.MirrorCS");var subQ5=sQuery(id+"F0.wireOp",EDGE,"E4.0.6.1");var subQ6=makeQuery(id+"F0.imprint","INTERSECT",VERTEX,{"derivedFrom":[subQ5,subQ3]});Q34=makeQuery(id+"F0.imprint","IMPRINT",FACE,{"disambiguationData":[TD([[makeQuery(id+"F0.imprint","IMPRINT",EDGE,{"disambiguationData":[TD([[subQ6,-1.0]])],"derivedFrom":subQ5}),-1.0]])]});}
            var Q35;
            {var subQ0=sQuery(id+"F0.wireOp",EDGE,"E18.MirrorCS");var subQ1=sQuery(id+"F0.wireOp",EDGE,"E4.0.8.0");var subQ2=makeQuery(id+"F0.imprint","INTERSECT",VERTEX,{"derivedFrom":[subQ1,subQ0]});Q35=makeQuery(id+"F0.imprint","IMPRINT",FACE,{"disambiguationData":[TD([[makeQuery(id+"F0.imprint","IMPRINT",EDGE,{"disambiguationData":[TD([[subQ2,-1.0]])],"derivedFrom":subQ1}),1.0]])]});}
            var Q36;
            {var subQ0=sQuery(id+"F0.wireOp",EDGE,"E18.MirrorCS");var subQ1=sQuery(id+"F0.wireOp",EDGE,"E0.right");var subQ2=makeQuery(id+"F0.imprint","INTERSECT",VERTEX,{"derivedFrom":[subQ1,subQ0]});Q36=makeQuery(id+"F0.imprint","IMPRINT",FACE,{"disambiguationData":[TD([[makeQuery(id+"F0.imprint","IMPRINT",EDGE,{"disambiguationData":[TD([[subQ2,-1.0]])],"derivedFrom":subQ1}),1.0]])]});}
            var Q37;
            {var subQ0=sQuery(id+"F0.wireOp",EDGE,"E4.0.8.0");var subQ1=sQuery(id+"F0.wireOp",EDGE,"E0.right");var subQ2=makeQuery(id+"F0.imprint","INTERSECT",VERTEX,{"derivedFrom":[subQ1,subQ0]});Q37=makeQuery(id+"F0.imprint","IMPRINT",FACE,{"disambiguationData":[TD([[makeQuery(id+"F0.imprint","IMPRINT",EDGE,{"disambiguationData":[TD([[subQ2,1.0]])],"derivedFrom":subQ1}),1.0]])]});}
            var Q38;
            {var subQ0=sQuery(id+"F0.wireOp",EDGE,"E20.MirrorCS");var subQ1=sQuery(id+"F0.wireOp",EDGE,"E4.0.8.0");var subQ2=makeQuery(id+"F0.imprint","INTERSECT",VERTEX,{"derivedFrom":[subQ1,subQ0]});Q38=makeQuery(id+"F0.imprint","IMPRINT",FACE,{"disambiguationData":[TD([[makeQuery(id+"F0.imprint","IMPRINT",EDGE,{"disambiguationData":[TD([[subQ2,-1.0]])],"derivedFrom":subQ1}),1.0]])]});}
            var Q39;
            {var subQ0=sQuery(id+"F0.wireOp",EDGE,"E20.MirrorCS");var subQ1=sQuery(id+"F0.wireOp",EDGE,"E4.0.9.0");var subQ2=makeQuery(id+"F0.imprint","INTERSECT",VERTEX,{"derivedFrom":[subQ1,subQ0]});Q39=makeQuery(id+"F0.imprint","IMPRINT",FACE,{"disambiguationData":[TD([[makeQuery(id+"F0.imprint","IMPRINT",EDGE,{"disambiguationData":[TD([[subQ2,-1.0]])],"derivedFrom":subQ1}),1.0]])]});}
            var Q40;
            {var subQ0=sQuery(id+"F0.wireOp",EDGE,"E21.MirrorCS");var subQ1=sQuery(id+"F0.wireOp",EDGE,"E0.right");var subQ2=makeQuery(id+"F0.imprint","INTERSECT",VERTEX,{"derivedFrom":[subQ1,subQ0]});Q40=makeQuery(id+"F0.imprint","IMPRINT",FACE,{"disambiguationData":[TD([[makeQuery(id+"F0.imprint","IMPRINT",EDGE,{"disambiguationData":[TD([[subQ2,1.0]])],"derivedFrom":subQ1}),1.0]])]});}
            var Q41;
            {var subQ0=sQuery(id+"F0.wireOp",EDGE,"E4.0.9.0");var subQ1=sQuery(id+"F0.wireOp",EDGE,"E0.right");var subQ2=makeQuery(id+"F0.imprint","INTERSECT",VERTEX,{"derivedFrom":[subQ1,subQ0]});Q41=makeQuery(id+"F0.imprint","IMPRINT",FACE,{"disambiguationData":[TD([[makeQuery(id+"F0.imprint","IMPRINT",EDGE,{"disambiguationData":[TD([[subQ2,1.0]])],"derivedFrom":subQ1}),1.0]])]});}
            var Q42;
            {var subQ0=sQuery(id+"F0.wireOp",EDGE,"E19.MirrorCS");var subQ1=sQuery(id+"F0.wireOp",EDGE,"E4.0.8.0");var subQ2=makeQuery(id+"F0.imprint","INTERSECT",VERTEX,{"derivedFrom":[subQ1,subQ0]});Q42=makeQuery(id+"F0.imprint","IMPRINT",FACE,{"disambiguationData":[TD([[makeQuery(id+"F0.imprint","IMPRINT",EDGE,{"disambiguationData":[TD([[subQ2,-1.0]])],"derivedFrom":subQ1}),1.0]])]});}
            var Q43;
            {var subQ0=sQuery(id+"F0.wireOp",EDGE,"E22.MirrorCS");var subQ1=sQuery(id+"F0.wireOp",EDGE,"E4.0.8.0");var subQ2=makeQuery(id+"F0.imprint","INTERSECT",VERTEX,{"derivedFrom":[subQ1,subQ0]});Q43=makeQuery(id+"F0.imprint","IMPRINT",FACE,{"disambiguationData":[TD([[makeQuery(id+"F0.imprint","IMPRINT",EDGE,{"disambiguationData":[TD([[subQ2,-1.0]])],"derivedFrom":subQ1}),1.0]])]});}
            var Q44;
            {var subQ0=sQuery(id+"F0.wireOp",EDGE,"E23.MirrorCS");var subQ1=sQuery(id+"F0.wireOp",EDGE,"E4.0.8.1");var subQ2=makeQuery(id+"F0.imprint","INTERSECT",VERTEX,{"derivedFrom":[subQ1,subQ0]});Q44=makeQuery(id+"F0.imprint","IMPRINT",FACE,{"disambiguationData":[TD([[makeQuery(id+"F0.imprint","IMPRINT",EDGE,{"disambiguationData":[TD([[subQ2,1.0]])],"derivedFrom":subQ1}),-1.0]])]});}
            var Q45;
            {var subQ3=sQuery(id+"F0.wireOp",EDGE,"E23.MirrorCS");var subQ5=sQuery(id+"F0.wireOp",EDGE,"E4.0.8.1");var subQ6=makeQuery(id+"F0.imprint","INTERSECT",VERTEX,{"derivedFrom":[subQ5,subQ3]});Q45=makeQuery(id+"F0.imprint","IMPRINT",FACE,{"disambiguationData":[TD([[makeQuery(id+"F0.imprint","IMPRINT",EDGE,{"disambiguationData":[TD([[subQ6,-1.0]])],"derivedFrom":subQ5}),-1.0]])]});}
            var Q46;
            {var subQ0=sQuery(id+"F0.wireOp",EDGE,"E21.MirrorCS");var subQ1=sQuery(id+"F0.wireOp",EDGE,"E4.0.8.0");var subQ2=makeQuery(id+"F0.imprint","INTERSECT",VERTEX,{"derivedFrom":[subQ1,subQ0]});Q46=makeQuery(id+"F0.imprint","IMPRINT",FACE,{"disambiguationData":[TD([[makeQuery(id+"F0.imprint","IMPRINT",EDGE,{"disambiguationData":[TD([[subQ2,-1.0]])],"derivedFrom":subQ1}),1.0]])]});}
            var Q47;
            {var subQ0=sQuery(id+"F0.wireOp",EDGE,"E24.MirrorCS");var subQ1=sQuery(id+"F0.wireOp",EDGE,"E4.0.8.0");var subQ2=makeQuery(id+"F0.imprint","INTERSECT",VERTEX,{"derivedFrom":[subQ1,subQ0]});Q47=makeQuery(id+"F0.imprint","IMPRINT",FACE,{"disambiguationData":[TD([[makeQuery(id+"F0.imprint","IMPRINT",EDGE,{"disambiguationData":[TD([[subQ2,-1.0]])],"derivedFrom":subQ1}),1.0]])]});}
            var Q48;
            {var subQ0=sQuery(id+"F0.wireOp",EDGE,"E25.MirrorCS");var subQ1=sQuery(id+"F0.wireOp",EDGE,"E4.0.8.0");var subQ2=makeQuery(id+"F0.imprint","INTERSECT",VERTEX,{"derivedFrom":[subQ1,subQ0]});Q48=makeQuery(id+"F0.imprint","IMPRINT",FACE,{"disambiguationData":[TD([[makeQuery(id+"F0.imprint","IMPRINT",EDGE,{"disambiguationData":[TD([[subQ2,-1.0]])],"derivedFrom":subQ1}),1.0]])]});}
            var Q49;
            {var subQ0=sQuery(id+"F0.wireOp",EDGE,"E26.MirrorCS");var subQ1=sQuery(id+"F0.wireOp",EDGE,"E4.0.8.0");var subQ2=makeQuery(id+"F0.imprint","INTERSECT",VERTEX,{"derivedFrom":[subQ1,subQ0]});Q49=makeQuery(id+"F0.imprint","IMPRINT",FACE,{"disambiguationData":[TD([[makeQuery(id+"F0.imprint","IMPRINT",EDGE,{"disambiguationData":[TD([[subQ2,-1.0]])],"derivedFrom":subQ1}),1.0]])]});}
            var Q50;
            {var subQ0=sQuery(id+"F0.wireOp",EDGE,"E4.0.8.0");var subQ1=sQuery(id+"F0.wireOp",EDGE,"E1.left");var subQ2=makeQuery(id+"F0.imprint","INTERSECT",VERTEX,{"derivedFrom":[subQ1,subQ0]});Q50=makeQuery(id+"F0.imprint","IMPRINT",FACE,{"disambiguationData":[TD([[makeQuery(id+"F0.imprint","IMPRINT",EDGE,{"disambiguationData":[TD([[subQ2,-1.0]])],"derivedFrom":subQ1}),1.0]])]});}
            var Q51;
            {var subQ0=sQuery(id+"F0.wireOp",EDGE,"E26.MirrorCS");var subQ1=sQuery(id+"F0.wireOp",EDGE,"E1.left");var subQ2=makeQuery(id+"F0.imprint","INTERSECT",VERTEX,{"derivedFrom":[subQ1,subQ0]});Q51=makeQuery(id+"F0.imprint","IMPRINT",FACE,{"disambiguationData":[TD([[makeQuery(id+"F0.imprint","IMPRINT",EDGE,{"disambiguationData":[TD([[subQ2,1.0]])],"derivedFrom":subQ1}),1.0]])]});}
            var Q52;
            {var subQ0=sQuery(id+"F0.wireOp",EDGE,"E22.MirrorCS");var subQ1=sQuery(id+"F0.wireOp",EDGE,"E4.0.9.0");var subQ2=makeQuery(id+"F0.imprint","INTERSECT",VERTEX,{"derivedFrom":[subQ1,subQ0]});Q52=makeQuery(id+"F0.imprint","IMPRINT",FACE,{"disambiguationData":[TD([[makeQuery(id+"F0.imprint","IMPRINT",EDGE,{"disambiguationData":[TD([[subQ2,-1.0]])],"derivedFrom":subQ1}),1.0]])]});}
            var Q53;
            {var subQ0=sQuery(id+"F0.wireOp",EDGE,"E22.MirrorCS");var subQ1=sQuery(id+"F0.wireOp",EDGE,"E4.0.10.0");var subQ2=makeQuery(id+"F0.imprint","INTERSECT",VERTEX,{"derivedFrom":[subQ1,subQ0]});Q53=makeQuery(id+"F0.imprint","IMPRINT",FACE,{"disambiguationData":[TD([[makeQuery(id+"F0.imprint","IMPRINT",EDGE,{"disambiguationData":[TD([[subQ2,-1.0]])],"derivedFrom":subQ1}),1.0]])]});}
            var Q54;
            {var subQ0=sQuery(id+"F0.wireOp",EDGE,"E22.MirrorCS");var subQ1=sQuery(id+"F0.wireOp",EDGE,"E0.right");var subQ2=makeQuery(id+"F0.imprint","INTERSECT",VERTEX,{"derivedFrom":[subQ1,subQ0]});Q54=makeQuery(id+"F0.imprint","IMPRINT",FACE,{"disambiguationData":[TD([[makeQuery(id+"F0.imprint","IMPRINT",EDGE,{"disambiguationData":[TD([[subQ2,-1.0]])],"derivedFrom":subQ1}),1.0]])]});}
            var Q55;
            {var subQ0=sQuery(id+"F0.wireOp",EDGE,"E4.0.10.0");var subQ1=sQuery(id+"F0.wireOp",EDGE,"E0.right");var subQ2=makeQuery(id+"F0.imprint","INTERSECT",VERTEX,{"derivedFrom":[subQ1,subQ0]});Q55=makeQuery(id+"F0.imprint","IMPRINT",FACE,{"disambiguationData":[TD([[makeQuery(id+"F0.imprint","IMPRINT",EDGE,{"disambiguationData":[TD([[subQ2,1.0]])],"derivedFrom":subQ1}),1.0]])]});}
            var Q56;
            {var subQ0=sQuery(id+"F0.wireOp",EDGE,"E21.MirrorCS");var subQ1=sQuery(id+"F0.wireOp",EDGE,"E4.0.9.0");var subQ2=makeQuery(id+"F0.imprint","INTERSECT",VERTEX,{"derivedFrom":[subQ1,subQ0]});Q56=makeQuery(id+"F0.imprint","IMPRINT",FACE,{"disambiguationData":[TD([[makeQuery(id+"F0.imprint","IMPRINT",EDGE,{"disambiguationData":[TD([[subQ2,-1.0]])],"derivedFrom":subQ1}),1.0]])]});}
            var Q57;
            {var subQ0=sQuery(id+"F0.wireOp",EDGE,"E24.MirrorCS");var subQ1=sQuery(id+"F0.wireOp",EDGE,"E0.right");var subQ2=makeQuery(id+"F0.imprint","INTERSECT",VERTEX,{"derivedFrom":[subQ1,subQ0]});Q57=makeQuery(id+"F0.imprint","IMPRINT",FACE,{"disambiguationData":[TD([[makeQuery(id+"F0.imprint","IMPRINT",EDGE,{"disambiguationData":[TD([[subQ2,-1.0]])],"derivedFrom":subQ1}),1.0]])]});}
            var Q58;
            Q58=makeQuery(id+"F1.opExtrude","CAP_FACE",FACE,{"disambiguationData":[OSD([sQuery(id+"F0.wireOp",EDGE,"E0.bottom"),sQuery(id+"F0.wireOp",EDGE,"E0.top"),sQuery(id+"F0.wireOp",EDGE,"E0.left"),sQuery(id+"F0.wireOp",EDGE,"E0.right"),sQuery(id+"F0.wireOp",EDGE,"E1.bottom"),sQuery(id+"F0.wireOp",EDGE,"E1.top"),sQuery(id+"F0.wireOp",EDGE,"E1.left"),sQuery(id+"F0.wireOp",EDGE,"E1.right"),sQuery(id+"F0.wireOp",EDGE,"E2"),sQuery(id+"F0.wireOp",EDGE,"E3"),sQuery(id+"F0.wireOp",EDGE,"E4.0.1.0"),sQuery(id+"F0.wireOp",EDGE,"E4.0.1.1"),sQuery(id+"F0.wireOp",EDGE,"E4.0.2.1"),sQuery(id+"F0.wireOp",EDGE,"E4.0.3.0"),sQuery(id+"F0.wireOp",EDGE,"E4.0.3.1"),sQuery(id+"F0.wireOp",EDGE,"E4.0.4.0"),sQuery(id+"F0.wireOp",EDGE,"E4.0.4.1"),sQuery(id+"F0.wireOp",EDGE,"E4.0.5.0"),sQuery(id+"F0.wireOp",EDGE,"E4.0.5.1"),sQuery(id+"F0.wireOp",EDGE,"E4.0.6.0"),sQuery(id+"F0.wireOp",EDGE,"E4.0.6.1"),sQuery(id+"F0.wireOp",EDGE,"E6.MirrorCS"),sQuery(id+"F0.wireOp",EDGE,"E7.MirrorCS"),sQuery(id+"F0.wireOp",EDGE,"E8.MirrorCS"),sQuery(id+"F0.wireOp",EDGE,"E9.MirrorCS"),sQuery(id+"F0.wireOp",EDGE,"E10.MirrorCS"),sQuery(id+"F0.wireOp",EDGE,"E11.MirrorCS"),sQuery(id+"F0.wireOp",EDGE,"E4.0.2.0"),sQuery(id+"F0.wireOp",EDGE,"E13.MirrorCS"),sQuery(id+"F0.wireOp",EDGE,"E14.MirrorCS"),sQuery(id+"F0.wireOp",EDGE,"E12.MirrorCS"),sQuery(id+"F0.wireOp",EDGE,"E17.MirrorCS"),sQuery(id+"F0.wireOp",EDGE,"E15.MirrorCS"),sQuery(id+"F0.wireOp",EDGE,"E18.MirrorCS"),sQuery(id+"F0.wireOp",EDGE,"E19.MirrorCS")])],"isStart":false});
            extrude(context, id + "F2", {"entities" : qUnion([Q0, Q1, Q2, Q3, Q4, Q5, Q6, Q7, Q8, Q9, Q10, Q11, Q12, Q13, Q14, Q15, Q16, Q17, Q18, Q19, Q20, Q21, Q22, Q23, Q24, Q25, Q26, Q27, Q28, Q29, Q30, Q31, Q32, Q33, Q34, Q35, Q36, Q37, Q38, Q39, Q40, Q41, Q42, Q43, Q44, Q45, Q46, Q47, Q48, Q49, Q50, Q51, Q52, Q53, Q54, Q55, Q56, Q57, Q58]), "operationType" : NewBodyOperationType.ADD, "depth" : 25.4 * mm});
        }
        {
            var Q0;
            {var subQ0=sQuery(id+"F0.wireOp",EDGE,"E23.MirrorCS");var subQ1=sQuery(id+"F0.wireOp",EDGE,"E4.0.10.0");var subQ2=makeQuery(id+"F0.imprint","INTERSECT",VERTEX,{"derivedFrom":[subQ1,subQ0]});Q0=makeQuery(id+"F0.imprint","IMPRINT",FACE,{"disambiguationData":[TD([[makeQuery(id+"F0.imprint","IMPRINT",EDGE,{"disambiguationData":[TD([[subQ2,-1.0]])],"derivedFrom":subQ1}),1.0]])]});}
            var Q1;
            {var subQ0=sQuery(id+"F0.wireOp",EDGE,"E4.0.11.0");var subQ1=sQuery(id+"F0.wireOp",EDGE,"E0.right");var subQ2=makeQuery(id+"F0.imprint","INTERSECT",VERTEX,{"derivedFrom":[subQ1,subQ0]});Q1=makeQuery(id+"F0.imprint","IMPRINT",FACE,{"disambiguationData":[TD([[makeQuery(id+"F0.imprint","IMPRINT",EDGE,{"disambiguationData":[TD([[subQ2,1.0]])],"derivedFrom":subQ1}),1.0]])]});}
            var Q2;
            {var subQ0=sQuery(id+"F0.wireOp",EDGE,"E24.MirrorCS");var subQ1=sQuery(id+"F0.wireOp",EDGE,"E4.0.11.0");var subQ2=makeQuery(id+"F0.imprint","INTERSECT",VERTEX,{"derivedFrom":[subQ1,subQ0]});Q2=makeQuery(id+"F0.imprint","IMPRINT",FACE,{"disambiguationData":[TD([[makeQuery(id+"F0.imprint","IMPRINT",EDGE,{"disambiguationData":[TD([[subQ2,-1.0]])],"derivedFrom":subQ1}),1.0]])]});}
            var Q3;
            {var subQ0=sQuery(id+"F0.wireOp",EDGE,"E25.MirrorCS");var subQ1=sQuery(id+"F0.wireOp",EDGE,"E4.0.11.0");var subQ2=makeQuery(id+"F0.imprint","INTERSECT",VERTEX,{"derivedFrom":[subQ1,subQ0]});Q3=makeQuery(id+"F0.imprint","IMPRINT",FACE,{"disambiguationData":[TD([[makeQuery(id+"F0.imprint","IMPRINT",EDGE,{"disambiguationData":[TD([[subQ2,-1.0]])],"derivedFrom":subQ1}),1.0]])]});}
            var Q4;
            {var subQ0=sQuery(id+"F0.wireOp",EDGE,"E26.MirrorCS");var subQ1=sQuery(id+"F0.wireOp",EDGE,"E4.0.11.0");var subQ2=makeQuery(id+"F0.imprint","INTERSECT",VERTEX,{"derivedFrom":[subQ1,subQ0]});Q4=makeQuery(id+"F0.imprint","IMPRINT",FACE,{"disambiguationData":[TD([[makeQuery(id+"F0.imprint","IMPRINT",EDGE,{"disambiguationData":[TD([[subQ2,-1.0]])],"derivedFrom":subQ1}),1.0]])]});}
            var Q5;
            {var subQ0=sQuery(id+"F0.wireOp",EDGE,"E27.MirrorCS");var subQ1=sQuery(id+"F0.wireOp",EDGE,"E4.0.11.0");var subQ2=makeQuery(id+"F0.imprint","INTERSECT",VERTEX,{"derivedFrom":[subQ1,subQ0]});Q5=makeQuery(id+"F0.imprint","IMPRINT",FACE,{"disambiguationData":[TD([[makeQuery(id+"F0.imprint","IMPRINT",EDGE,{"disambiguationData":[TD([[subQ2,-1.0]])],"derivedFrom":subQ1}),1.0]])]});}
            var Q6;
            {var subQ0=sQuery(id+"F0.wireOp",EDGE,"E28.MirrorCS");var subQ1=sQuery(id+"F0.wireOp",EDGE,"E4.0.11.0");var subQ2=makeQuery(id+"F0.imprint","INTERSECT",VERTEX,{"derivedFrom":[subQ1,subQ0]});Q6=makeQuery(id+"F0.imprint","IMPRINT",FACE,{"disambiguationData":[TD([[makeQuery(id+"F0.imprint","IMPRINT",EDGE,{"disambiguationData":[TD([[subQ2,-1.0]])],"derivedFrom":subQ1}),1.0]])]});}
            var Q7;
            {var subQ0=sQuery(id+"F0.wireOp",EDGE,"E29.MirrorCS");var subQ1=sQuery(id+"F0.wireOp",EDGE,"E4.0.11.1");var subQ2=makeQuery(id+"F0.imprint","INTERSECT",VERTEX,{"derivedFrom":[subQ1,subQ0]});Q7=makeQuery(id+"F0.imprint","IMPRINT",FACE,{"disambiguationData":[TD([[makeQuery(id+"F0.imprint","IMPRINT",EDGE,{"disambiguationData":[TD([[subQ2,1.0]])],"derivedFrom":subQ1}),-1.0]])]});}
            var Q8;
            {var subQ0=sQuery(id+"F0.wireOp",EDGE,"E4.0.11.0");var subQ1=sQuery(id+"F0.wireOp",EDGE,"E1.left");var subQ2=makeQuery(id+"F0.imprint","INTERSECT",VERTEX,{"derivedFrom":[subQ1,subQ0]});Q8=makeQuery(id+"F0.imprint","IMPRINT",FACE,{"disambiguationData":[TD([[makeQuery(id+"F0.imprint","IMPRINT",EDGE,{"disambiguationData":[TD([[subQ2,-1.0]])],"derivedFrom":subQ1}),1.0]])]});}
            var Q9;
            {var subQ0=sQuery(id+"F0.wireOp",EDGE,"E4.0.10.0");var subQ1=sQuery(id+"F0.wireOp",EDGE,"E1.left");var subQ2=makeQuery(id+"F0.imprint","INTERSECT",VERTEX,{"derivedFrom":[subQ1,subQ0]});Q9=makeQuery(id+"F0.imprint","IMPRINT",FACE,{"disambiguationData":[TD([[makeQuery(id+"F0.imprint","IMPRINT",EDGE,{"disambiguationData":[TD([[subQ2,-1.0]])],"derivedFrom":subQ1}),1.0]])]});}
            var Q10;
            {var subQ0=sQuery(id+"F0.wireOp",EDGE,"E28.MirrorCS");var subQ1=sQuery(id+"F0.wireOp",EDGE,"E4.0.10.0");var subQ2=makeQuery(id+"F0.imprint","INTERSECT",VERTEX,{"derivedFrom":[subQ1,subQ0]});Q10=makeQuery(id+"F0.imprint","IMPRINT",FACE,{"disambiguationData":[TD([[makeQuery(id+"F0.imprint","IMPRINT",EDGE,{"disambiguationData":[TD([[subQ2,-1.0]])],"derivedFrom":subQ1}),1.0]])]});}
            var Q11;
            {var subQ3=sQuery(id+"F0.wireOp",EDGE,"E27.MirrorCS");var subQ5=sQuery(id+"F0.wireOp",EDGE,"E4.0.10.1");var subQ6=makeQuery(id+"F0.imprint","INTERSECT",VERTEX,{"derivedFrom":[subQ5,subQ3]});Q11=makeQuery(id+"F0.imprint","IMPRINT",FACE,{"disambiguationData":[TD([[makeQuery(id+"F0.imprint","IMPRINT",EDGE,{"disambiguationData":[TD([[subQ6,-1.0]])],"derivedFrom":subQ5}),-1.0]])]});}
            var Q12;
            {var subQ0=sQuery(id+"F0.wireOp",EDGE,"E27.MirrorCS");var subQ1=sQuery(id+"F0.wireOp",EDGE,"E4.0.10.1");var subQ2=makeQuery(id+"F0.imprint","INTERSECT",VERTEX,{"derivedFrom":[subQ1,subQ0]});Q12=makeQuery(id+"F0.imprint","IMPRINT",FACE,{"disambiguationData":[TD([[makeQuery(id+"F0.imprint","IMPRINT",EDGE,{"disambiguationData":[TD([[subQ2,1.0]])],"derivedFrom":subQ1}),-1.0]])]});}
            var Q13;
            {var subQ0=sQuery(id+"F0.wireOp",EDGE,"E26.MirrorCS");var subQ1=sQuery(id+"F0.wireOp",EDGE,"E4.0.10.0");var subQ2=makeQuery(id+"F0.imprint","INTERSECT",VERTEX,{"derivedFrom":[subQ1,subQ0]});Q13=makeQuery(id+"F0.imprint","IMPRINT",FACE,{"disambiguationData":[TD([[makeQuery(id+"F0.imprint","IMPRINT",EDGE,{"disambiguationData":[TD([[subQ2,-1.0]])],"derivedFrom":subQ1}),1.0]])]});}
            var Q14;
            {var subQ0=sQuery(id+"F0.wireOp",EDGE,"E25.MirrorCS");var subQ1=sQuery(id+"F0.wireOp",EDGE,"E4.0.10.0");var subQ2=makeQuery(id+"F0.imprint","INTERSECT",VERTEX,{"derivedFrom":[subQ1,subQ0]});Q14=makeQuery(id+"F0.imprint","IMPRINT",FACE,{"disambiguationData":[TD([[makeQuery(id+"F0.imprint","IMPRINT",EDGE,{"disambiguationData":[TD([[subQ2,-1.0]])],"derivedFrom":subQ1}),1.0]])]});}
            var Q15;
            {var subQ0=sQuery(id+"F0.wireOp",EDGE,"E24.MirrorCS");var subQ1=sQuery(id+"F0.wireOp",EDGE,"E4.0.10.0");var subQ2=makeQuery(id+"F0.imprint","INTERSECT",VERTEX,{"derivedFrom":[subQ1,subQ0]});Q15=makeQuery(id+"F0.imprint","IMPRINT",FACE,{"disambiguationData":[TD([[makeQuery(id+"F0.imprint","IMPRINT",EDGE,{"disambiguationData":[TD([[subQ2,-1.0]])],"derivedFrom":subQ1}),1.0]])]});}
            var Q16;
            {var subQ0=sQuery(id+"F0.wireOp",EDGE,"E23.MirrorCS");var subQ1=sQuery(id+"F0.wireOp",EDGE,"E4.0.9.0");var subQ2=makeQuery(id+"F0.imprint","INTERSECT",VERTEX,{"derivedFrom":[subQ1,subQ0]});Q16=makeQuery(id+"F0.imprint","IMPRINT",FACE,{"disambiguationData":[TD([[makeQuery(id+"F0.imprint","IMPRINT",EDGE,{"disambiguationData":[TD([[subQ2,-1.0]])],"derivedFrom":subQ1}),1.0]])]});}
            var Q17;
            {var subQ0=sQuery(id+"F0.wireOp",EDGE,"E24.MirrorCS");var subQ1=sQuery(id+"F0.wireOp",EDGE,"E4.0.9.0");var subQ2=makeQuery(id+"F0.imprint","INTERSECT",VERTEX,{"derivedFrom":[subQ1,subQ0]});Q17=makeQuery(id+"F0.imprint","IMPRINT",FACE,{"disambiguationData":[TD([[makeQuery(id+"F0.imprint","IMPRINT",EDGE,{"disambiguationData":[TD([[subQ2,-1.0]])],"derivedFrom":subQ1}),1.0]])]});}
            var Q18;
            {var subQ3=sQuery(id+"F0.wireOp",EDGE,"E25.MirrorCS");var subQ5=sQuery(id+"F0.wireOp",EDGE,"E4.0.9.1");var subQ6=makeQuery(id+"F0.imprint","INTERSECT",VERTEX,{"derivedFrom":[subQ5,subQ3]});Q18=makeQuery(id+"F0.imprint","IMPRINT",FACE,{"disambiguationData":[TD([[makeQuery(id+"F0.imprint","IMPRINT",EDGE,{"disambiguationData":[TD([[subQ6,-1.0]])],"derivedFrom":subQ5}),-1.0]])]});}
            var Q19;
            {var subQ0=sQuery(id+"F0.wireOp",EDGE,"E25.MirrorCS");var subQ1=sQuery(id+"F0.wireOp",EDGE,"E4.0.9.1");var subQ2=makeQuery(id+"F0.imprint","INTERSECT",VERTEX,{"derivedFrom":[subQ1,subQ0]});Q19=makeQuery(id+"F0.imprint","IMPRINT",FACE,{"disambiguationData":[TD([[makeQuery(id+"F0.imprint","IMPRINT",EDGE,{"disambiguationData":[TD([[subQ2,1.0]])],"derivedFrom":subQ1}),-1.0]])]});}
            var Q20;
            {var subQ0=sQuery(id+"F0.wireOp",EDGE,"E27.MirrorCS");var subQ1=sQuery(id+"F0.wireOp",EDGE,"E4.0.9.0");var subQ2=makeQuery(id+"F0.imprint","INTERSECT",VERTEX,{"derivedFrom":[subQ1,subQ0]});Q20=makeQuery(id+"F0.imprint","IMPRINT",FACE,{"disambiguationData":[TD([[makeQuery(id+"F0.imprint","IMPRINT",EDGE,{"disambiguationData":[TD([[subQ2,-1.0]])],"derivedFrom":subQ1}),1.0]])]});}
            var Q21;
            {var subQ0=sQuery(id+"F0.wireOp",EDGE,"E28.MirrorCS");var subQ1=sQuery(id+"F0.wireOp",EDGE,"E4.0.9.0");var subQ2=makeQuery(id+"F0.imprint","INTERSECT",VERTEX,{"derivedFrom":[subQ1,subQ0]});Q21=makeQuery(id+"F0.imprint","IMPRINT",FACE,{"disambiguationData":[TD([[makeQuery(id+"F0.imprint","IMPRINT",EDGE,{"disambiguationData":[TD([[subQ2,-1.0]])],"derivedFrom":subQ1}),1.0]])]});}
            var Q22;
            {var subQ0=sQuery(id+"F0.wireOp",EDGE,"E4.0.9.0");var subQ1=sQuery(id+"F0.wireOp",EDGE,"E1.left");var subQ2=makeQuery(id+"F0.imprint","INTERSECT",VERTEX,{"derivedFrom":[subQ1,subQ0]});Q22=makeQuery(id+"F0.imprint","IMPRINT",FACE,{"disambiguationData":[TD([[makeQuery(id+"F0.imprint","IMPRINT",EDGE,{"disambiguationData":[TD([[subQ2,-1.0]])],"derivedFrom":subQ1}),1.0]])]});}
            var Q23;
            {var subQ0=sQuery(id+"F0.wireOp",EDGE,"E26.MirrorCS");var subQ1=sQuery(id+"F0.wireOp",EDGE,"E4.0.9.0");var subQ2=makeQuery(id+"F0.imprint","INTERSECT",VERTEX,{"derivedFrom":[subQ1,subQ0]});Q23=makeQuery(id+"F0.imprint","IMPRINT",FACE,{"disambiguationData":[TD([[makeQuery(id+"F0.imprint","IMPRINT",EDGE,{"disambiguationData":[TD([[subQ2,-1.0]])],"derivedFrom":subQ1}),1.0]])]});}
            var Q24;
            {var subQ0=sQuery(id+"F0.wireOp",EDGE,"E24.MirrorCS");var subQ1=sQuery(id+"F0.wireOp",EDGE,"E0.right");var subQ2=makeQuery(id+"F0.imprint","INTERSECT",VERTEX,{"derivedFrom":[subQ1,subQ0]});Q24=makeQuery(id+"F0.imprint","IMPRINT",FACE,{"disambiguationData":[TD([[makeQuery(id+"F0.imprint","IMPRINT",EDGE,{"disambiguationData":[TD([[subQ2,-1.0]])],"derivedFrom":subQ1}),1.0]])]});}
            var Q25;
            {var subQ0=sQuery(id+"F0.wireOp",EDGE,"E26.MirrorCS");var subQ1=sQuery(id+"F0.wireOp",EDGE,"E0.right");var subQ2=makeQuery(id+"F0.imprint","INTERSECT",VERTEX,{"derivedFrom":[subQ1,subQ0]});Q25=makeQuery(id+"F0.imprint","IMPRINT",FACE,{"disambiguationData":[TD([[makeQuery(id+"F0.imprint","IMPRINT",EDGE,{"disambiguationData":[TD([[subQ2,-1.0]])],"derivedFrom":subQ1}),1.0]])]});}
            var Q26;
            {var subQ0=sQuery(id+"F0.wireOp",EDGE,"E28.MirrorCS");var subQ1=sQuery(id+"F0.wireOp",EDGE,"E1.left");var subQ2=makeQuery(id+"F0.imprint","INTERSECT",VERTEX,{"derivedFrom":[subQ1,subQ0]});Q26=makeQuery(id+"F0.imprint","IMPRINT",FACE,{"disambiguationData":[TD([[makeQuery(id+"F0.imprint","IMPRINT",EDGE,{"disambiguationData":[TD([[subQ2,1.0]])],"derivedFrom":subQ1}),1.0]])]});}
            var Q27;
            {var subQ0=sQuery(id+"F0.wireOp",EDGE,"E28.MirrorCS");var subQ1=sQuery(id+"F0.wireOp",EDGE,"E0.right");var subQ2=makeQuery(id+"F0.imprint","INTERSECT",VERTEX,{"derivedFrom":[subQ1,subQ0]});Q27=makeQuery(id+"F0.imprint","IMPRINT",FACE,{"disambiguationData":[TD([[makeQuery(id+"F0.imprint","IMPRINT",EDGE,{"disambiguationData":[TD([[subQ2,-1.0]])],"derivedFrom":subQ1}),1.0]])]});}
            extrude(context, id + "F3", {"entities" : qUnion([Q0, Q1, Q2, Q3, Q4, Q5, Q6, Q7, Q8, Q9, Q10, Q11, Q12, Q13, Q14, Q15, Q16, Q17, Q18, Q19, Q20, Q21, Q22, Q23, Q24, Q25, Q26, Q27]), "operationType" : NewBodyOperationType.ADD, "depth" : 25.4 * mm});
        }
        {
            var Q0;
            Q0=qCreatedBy(makeId("Top.planeOp"),FACE);
            var sketch = newSketch(context, id + "F4", { "sketchPlane" : qUnion([Q0])});
            skCircle(sketch, "E30", {"center": v(0, 0) * mm, "radius": 355.6 * mm});
            skCircle(sketch, "E31", {"center": v(0, 355.6) * mm, "radius": 355.6 * mm});
            skCircle(sketch, "E32", {"center": v(-307.96, 177.8) * mm, "radius": 355.6 * mm});
            skSolve(sketch);
        }
        {
            var Q0;
            Q0=makeQuery(id+"F1.opExtrude","SWEPT_BODY",BODY,{"disambiguationData":[OSD([sQuery(id+"F0.wireOp",EDGE,"E0.bottom"),sQuery(id+"F0.wireOp",EDGE,"E0.top"),sQuery(id+"F0.wireOp",EDGE,"E0.left"),sQuery(id+"F0.wireOp",EDGE,"E0.right"),sQuery(id+"F0.wireOp",EDGE,"E1.bottom"),sQuery(id+"F0.wireOp",EDGE,"E1.top"),sQuery(id+"F0.wireOp",EDGE,"E1.left"),sQuery(id+"F0.wireOp",EDGE,"E1.right"),sQuery(id+"F0.wireOp",EDGE,"E2"),sQuery(id+"F0.wireOp",EDGE,"E3"),sQuery(id+"F0.wireOp",EDGE,"E4.0.1.0"),sQuery(id+"F0.wireOp",EDGE,"E4.0.1.1"),sQuery(id+"F0.wireOp",EDGE,"E4.0.2.1"),sQuery(id+"F0.wireOp",EDGE,"E4.0.3.0"),sQuery(id+"F0.wireOp",EDGE,"E4.0.3.1"),sQuery(id+"F0.wireOp",EDGE,"E4.0.4.0"),sQuery(id+"F0.wireOp",EDGE,"E4.0.4.1"),sQuery(id+"F0.wireOp",EDGE,"E4.0.5.0"),sQuery(id+"F0.wireOp",EDGE,"E4.0.5.1"),sQuery(id+"F0.wireOp",EDGE,"E4.0.6.0"),sQuery(id+"F0.wireOp",EDGE,"E4.0.6.1"),sQuery(id+"F0.wireOp",EDGE,"E6.MirrorCS"),sQuery(id+"F0.wireOp",EDGE,"E7.MirrorCS"),sQuery(id+"F0.wireOp",EDGE,"E8.MirrorCS"),sQuery(id+"F0.wireOp",EDGE,"E9.MirrorCS"),sQuery(id+"F0.wireOp",EDGE,"E10.MirrorCS"),sQuery(id+"F0.wireOp",EDGE,"E11.MirrorCS"),sQuery(id+"F0.wireOp",EDGE,"E4.0.2.0"),sQuery(id+"F0.wireOp",EDGE,"E13.MirrorCS"),sQuery(id+"F0.wireOp",EDGE,"E14.MirrorCS"),sQuery(id+"F0.wireOp",EDGE,"E12.MirrorCS"),sQuery(id+"F0.wireOp",EDGE,"E17.MirrorCS"),sQuery(id+"F0.wireOp",EDGE,"E15.MirrorCS"),sQuery(id+"F0.wireOp",EDGE,"E16.MirrorCS"),sQuery(id+"F0.wireOp",EDGE,"E18.MirrorCS"),sQuery(id+"F0.wireOp",EDGE,"E19.MirrorCS")])]});
            var Q1;
            Q1=sQuery(id+"F4.wireOp",EDGE,"E30");
            circularPattern(context, id + "F5", {"entities" : qUnion([Q0]), "axis" : qUnion([Q1]), "angle" : 60 * degree, "instanceCount" : 2});
        }
        {
            var Q0;
            Q0=makeQuery(id+"F1.opExtrude","SWEPT_BODY",BODY,{"disambiguationData":[OSD([sQuery(id+"F0.wireOp",EDGE,"E0.bottom"),sQuery(id+"F0.wireOp",EDGE,"E0.top"),sQuery(id+"F0.wireOp",EDGE,"E0.left"),sQuery(id+"F0.wireOp",EDGE,"E0.right"),sQuery(id+"F0.wireOp",EDGE,"E1.bottom"),sQuery(id+"F0.wireOp",EDGE,"E1.top"),sQuery(id+"F0.wireOp",EDGE,"E1.left"),sQuery(id+"F0.wireOp",EDGE,"E1.right"),sQuery(id+"F0.wireOp",EDGE,"E2"),sQuery(id+"F0.wireOp",EDGE,"E3"),sQuery(id+"F0.wireOp",EDGE,"E4.0.1.0"),sQuery(id+"F0.wireOp",EDGE,"E4.0.1.1"),sQuery(id+"F0.wireOp",EDGE,"E4.0.2.1"),sQuery(id+"F0.wireOp",EDGE,"E4.0.3.0"),sQuery(id+"F0.wireOp",EDGE,"E4.0.3.1"),sQuery(id+"F0.wireOp",EDGE,"E4.0.4.0"),sQuery(id+"F0.wireOp",EDGE,"E4.0.4.1"),sQuery(id+"F0.wireOp",EDGE,"E4.0.5.0"),sQuery(id+"F0.wireOp",EDGE,"E4.0.5.1"),sQuery(id+"F0.wireOp",EDGE,"E4.0.6.0"),sQuery(id+"F0.wireOp",EDGE,"E4.0.6.1"),sQuery(id+"F0.wireOp",EDGE,"E6.MirrorCS"),sQuery(id+"F0.wireOp",EDGE,"E7.MirrorCS"),sQuery(id+"F0.wireOp",EDGE,"E8.MirrorCS"),sQuery(id+"F0.wireOp",EDGE,"E9.MirrorCS"),sQuery(id+"F0.wireOp",EDGE,"E10.MirrorCS"),sQuery(id+"F0.wireOp",EDGE,"E11.MirrorCS"),sQuery(id+"F0.wireOp",EDGE,"E4.0.2.0"),sQuery(id+"F0.wireOp",EDGE,"E13.MirrorCS"),sQuery(id+"F0.wireOp",EDGE,"E14.MirrorCS"),sQuery(id+"F0.wireOp",EDGE,"E12.MirrorCS"),sQuery(id+"F0.wireOp",EDGE,"E17.MirrorCS"),sQuery(id+"F0.wireOp",EDGE,"E15.MirrorCS"),sQuery(id+"F0.wireOp",EDGE,"E16.MirrorCS"),sQuery(id+"F0.wireOp",EDGE,"E18.MirrorCS"),sQuery(id+"F0.wireOp",EDGE,"E19.MirrorCS")])]});
            var Q1;
            Q1=sQuery(id+"F4.wireOp",EDGE,"E31");
            circularPattern(context, id + "F6", {"entities" : qUnion([Q0]), "axis" : qUnion([Q1]), "angle" : 60 * degree, "instanceCount" : 2, "oppositeDirection" : true});
        }
        {
            var Q0;
            {var subQ0=sQuery(id+"F0.wireOp",EDGE,"E0.bottom");Q0=makeQuery(id+"F6.opPattern","COPY",FACE,{"derivedFrom":makeQuery(id+"F2.boolean.opBoolean","MERGE",FACE,{"derivedFrom":[makeQuery(id+"F1.opExtrude","SWEPT_FACE",FACE,{"disambiguationData":[OSD([subQ0])]}),makeQuery(id+"F2.opExtrude","SWEPT_FACE",FACE,{"disambiguationData":[OSD([subQ0])]})]}),"instanceName":"1"});}
            var sketch = newSketch(context, id + "F7", { "sketchPlane" : qUnion([Q0])});
            skCircle(sketch, "E33", {"center": v(-79.36, 177.8) * mm, "radius": 254 * mm});
            skSolve(sketch);
        }
        {
            var Q0;
            Q0 = qSketchRegion(id + "F7", true);
            extrude(context, id + "F8", {"entities" : qUnion([Q0]), "operationType" : NewBodyOperationType.ADD, "depth" : 1016 * mm, "hasDraft" : true, "draftAngle" : 10 * degree, "draftPullDirection" : true});
        }
    });
